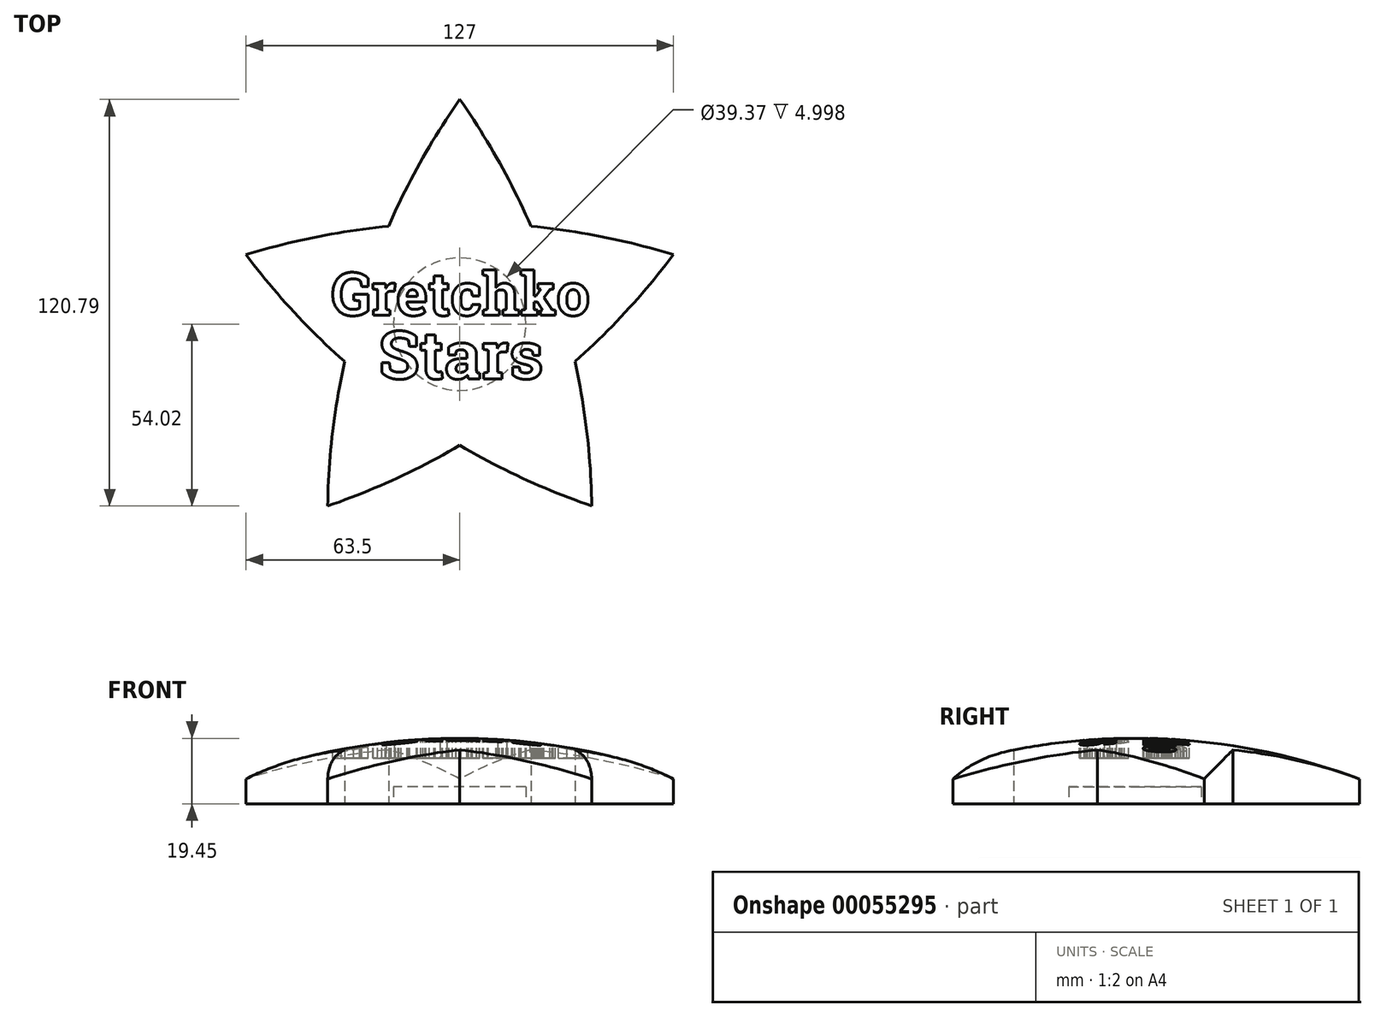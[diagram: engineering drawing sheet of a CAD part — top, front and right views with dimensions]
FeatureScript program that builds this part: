
annotation { "Feature Type Name" : "Feature", "Feature Type Description" : "" }
export const myFeature = defineFeature(function(context is Context, id is Id, definition is map)
    precondition{}
    {
        {
            var Q0;
            Q0=qCreatedBy(makeId("Top.planeOp"),FACE);
            var sketch = newSketch(context, id + "F0", { "sketchPlane" : qUnion([Q0])});
            skArc(sketch, "E0", {"start": v(39.25, -54.02) * mm, "mid": v(28.67, 9.31) * mm, "end": v(0, 66.77) * mm});
            skArc(sketch, "E1", {"start": v(0, 66.77) * mm, "mid": v(-28.67, 9.31) * mm, "end": v(-39.25, -54.02) * mm});
            skArc(sketch, "E2", {"start": v(63.5, 20.63) * mm, "mid": v(0, 30.14) * mm, "end": v(-63.5, 20.63) * mm});
            skArc(sketch, "E3", {"start": v(-63.5, 20.63) * mm, "mid": v(-17.72, -24.39) * mm, "end": v(39.25, -54.02) * mm});
            skArc(sketch, "E4", {"start": v(-39.25, -54.02) * mm, "mid": v(17.72, -24.39) * mm, "end": v(63.5, 20.63) * mm});
            skSolve(sketch);
        }
        {
            var Q0;
            Q0=qSketchRegion(id+"F0",true);
            extrude(context, id + "F1", {"entities" : qUnion([Q0]), "depth" : 67.5 * mm});
        }
        {
            var Q0;
            Q0=qCreatedBy(makeId("Top.planeOp"),FACE);
            var sketch = newSketch(context, id + "F2", { "sketchPlane" : qUnion([Q0])});
            skCircle(sketch, "E5", {"center": v(0, 0) * mm, "radius": 190.5 * mm});
            skLineSegment(sketch, "E6", {"start": v(0, 190.5) * mm, "end": v(0, -190.5) * mm});
            skSolve(sketch);
        }
        {
            var Q0;
            Q0=makeQuery(id+"F1.opExtrude","SWEPT_BODY",BODY,{"disambiguationData":[OSD([sQuery(id+"F0.wireOp",EDGE,"E0"),sQuery(id+"F0.wireOp",EDGE,"E1"),sQuery(id+"F0.wireOp",EDGE,"E2"),sQuery(id+"F0.wireOp",EDGE,"E3"),sQuery(id+"F0.wireOp",EDGE,"E4")])]});
            var Q1;
            Q1=makeQuery(id+"F1.opExtrude","SWEPT_EDGE",EDGE,{"disambiguationData":[OSD([sQuery(id+"F0.wireOp",EDGE,"E2"),sQuery(id+"F0.wireOp",EDGE,"E3")])]});
            var Q2;
            Q2=makeQuery(id+"F1.opExtrude","CAP_FACE",FACE,{"disambiguationData":[OSD([sQuery(id+"F0.wireOp",EDGE,"E0"),sQuery(id+"F0.wireOp",EDGE,"E1"),sQuery(id+"F0.wireOp",EDGE,"E2"),sQuery(id+"F0.wireOp",EDGE,"E3"),sQuery(id+"F0.wireOp",EDGE,"E4")])],"isStart":false});
            transform(context, id + "F3", {"entities" : qUnion([Q0]), "transformType" : TransformType.TRANSLATION_DISTANCE, "transformDirection" : qUnion([Q2]), "distance" : 171.05 * mm, "makeCopy" : false});
        }
        {
            var Q0;
            {var subQ0=sQuery(id+"F2.wireOp",EDGE,"E6");Q0=makeQuery(id+"F2.imprint","IMPRINT",FACE,{"disambiguationData":[TD([[makeQuery(id+"F2.imprint","IMPRINT",EDGE,{"derivedFrom":subQ0}),-1.0]])]});}
            var Q1;
            Q1=sQuery(id+"F2.wireOp",EDGE,"E6");
            revolve(context, id + "F4", {"entities" : qUnion([Q0]), "axis" : qUnion([Q1]), "revolveType" : RevolveType.FULL});
        }
        {
            var Q0;
            Q0=makeQuery(id+"F1.opExtrude","SWEPT_BODY",BODY,{"disambiguationData":[OSD([sQuery(id+"F0.wireOp",EDGE,"E0"),sQuery(id+"F0.wireOp",EDGE,"E1"),sQuery(id+"F0.wireOp",EDGE,"E2"),sQuery(id+"F0.wireOp",EDGE,"E3"),sQuery(id+"F0.wireOp",EDGE,"E4")])]});
            var Q1;
            Q1=makeQuery(id+"F4.opRevolve","SWEPT_BODY",BODY,{"disambiguationData":[OSD([sQuery(id+"F2.wireOp",EDGE,"E5"),sQuery(id+"F2.wireOp",EDGE,"E6")])]});
            booleanBodies(context, id + "F5", {"operationType" : BooleanOperationType.INTERSECTION, "tools" : qUnion([Q0, Q1])});
        }
        {
            var Q0;
            Q0=qCreatedBy(makeId("Top.planeOp"),FACE);
            var sketch = newSketch(context, id + "F6", { "sketchPlane" : qUnion([Q0])});
            skText(sketch, "E7", { "text": "Gretchko", "fontName": "RobotoSlab-Bold.ttf"});
            skLineSegment(sketch, "E8", {"start": v(0, 0) * mm, "end": v(0, 66.71) * mm});
            const initialGuessF6  = {"E7": [-0.03813, 0.00261, 1, 0, 0.0128]};
            skSetInitialGuess(sketch, initialGuessF6);
            skSolve(sketch);
        }
        {
            var Q0;
            Q0=qCreatedBy(makeId("Top.planeOp"),FACE);
            var sketch = newSketch(context, id + "F7", { "sketchPlane" : qUnion([Q0])});
            skText(sketch, "E9", { "text": "Stars", "fontName": "RobotoSlab-Bold.ttf"});
            const initialGuessF7  = {"E9": [-0.02408, -0.01622, 1, 0, 0.01428]};
            skSetInitialGuess(sketch, initialGuessF7);
            skSolve(sketch);
        }
        {
            var Q0;
            Q0=makeQuery(id+"F5.opBoolean","INTERSECT",BODY,{"derivedFrom":[makeQuery(id+"F1.opExtrude","SWEPT_BODY",BODY,{"disambiguationData":[OSD([sQuery(id+"F0.wireOp",EDGE,"E0"),sQuery(id+"F0.wireOp",EDGE,"E1"),sQuery(id+"F0.wireOp",EDGE,"E2"),sQuery(id+"F0.wireOp",EDGE,"E3"),sQuery(id+"F0.wireOp",EDGE,"E4")])]}),makeQuery(id+"F4.opRevolve","SWEPT_BODY",BODY,{"disambiguationData":[OSD([sQuery(id+"F2.wireOp",EDGE,"E5"),sQuery(id+"F2.wireOp",EDGE,"E6")])]})]});
            var Q1;
            Q1=qCreatedBy(makeId("Top.planeOp"),FACE);
            transform(context, id + "F8", {"entities" : qUnion([Q0]), "transformType" : TransformType.TRANSLATION_DISTANCE, "transformDirection" : qUnion([Q1]), "distance" : 221.94 * mm, "oppositeDirection" : true, "makeCopy" : false});
        }
        {
            var Q0;
            Q0=makeQuery(id+"F6.imprint","IMPRINT",FACE,{"disambiguationData":[TD([[makeQuery(id+"F6.imprint","IMPRINT",EDGE,{"derivedFrom":sQuery(id+"F6.wireOp",EDGE,"E7.sketch_text.stroke-0")}),-1.0]])]});
            var Q1;
            Q1=makeQuery(id+"F6.imprint","IMPRINT",FACE,{"disambiguationData":[TD([[makeQuery(id+"F6.imprint","IMPRINT",EDGE,{"derivedFrom":sQuery(id+"F6.wireOp",EDGE,"E7.sketch_text.stroke-26")}),-1.0]])]});
            var Q2;
            Q2=makeQuery(id+"F6.imprint","IMPRINT",FACE,{"disambiguationData":[TD([[makeQuery(id+"F6.imprint","IMPRINT",EDGE,{"derivedFrom":sQuery(id+"F6.wireOp",EDGE,"E7.sketch_text.stroke-69")}),-1.0]])]});
            var Q3;
            Q3=makeQuery(id+"F6.imprint","IMPRINT",FACE,{"disambiguationData":[TD([[makeQuery(id+"F6.imprint","IMPRINT",EDGE,{"derivedFrom":sQuery(id+"F6.wireOp",EDGE,"E7.sketch_text.stroke-112")}),-1.0]])]});
            var Q4;
            Q4=makeQuery(id+"F6.imprint","IMPRINT",FACE,{"disambiguationData":[TD([[makeQuery(id+"F6.imprint","IMPRINT",EDGE,{"derivedFrom":sQuery(id+"F6.wireOp",EDGE,"E7.sketch_text.stroke-138")}),-1.0]])]});
            var Q5;
            Q5=makeQuery(id+"F6.imprint","IMPRINT",FACE,{"disambiguationData":[TD([[makeQuery(id+"F6.imprint","IMPRINT",EDGE,{"derivedFrom":sQuery(id+"F6.wireOp",EDGE,"E7.sketch_text.stroke-45")}),-1.0]])]});
            var Q6;
            Q6=makeQuery(id+"F6.imprint","IMPRINT",FACE,{"disambiguationData":[TD([[makeQuery(id+"F6.imprint","IMPRINT",EDGE,{"derivedFrom":sQuery(id+"F6.wireOp",EDGE,"E7.sketch_text.stroke-89")}),-1.0]])]});
            var Q7;
            {var subQ1=sQuery(id+"F6.wireOp",EDGE,"E7.sketch_text.stroke-96");Q7=makeQuery(id+"F6.imprint","IMPRINT",FACE,{"disambiguationData":[TD([[makeQuery(id+"F6.imprint","IMPRINT",EDGE,{"derivedFrom":subQ1}),-1.0]])]});}
            var Q8;
            Q8=makeQuery(id+"F6.imprint","IMPRINT",FACE,{"disambiguationData":[TD([[makeQuery(id+"F6.imprint","IMPRINT",EDGE,{"derivedFrom":sQuery(id+"F6.wireOp",EDGE,"E7.sketch_text.stroke-165")}),-1.0]])]});
            var Q9;
            Q9=makeQuery(id+"F7.imprint","IMPRINT",FACE,{"disambiguationData":[TD([[makeQuery(id+"F7.imprint","IMPRINT",EDGE,{"derivedFrom":sQuery(id+"F7.wireOp",EDGE,"E9.sketch_text.stroke-0")}),-1.0]])]});
            var Q10;
            Q10=makeQuery(id+"F7.imprint","IMPRINT",FACE,{"disambiguationData":[TD([[makeQuery(id+"F7.imprint","IMPRINT",EDGE,{"derivedFrom":sQuery(id+"F7.wireOp",EDGE,"E9.sketch_text.stroke-30")}),-1.0]])]});
            var Q11;
            Q11=makeQuery(id+"F7.imprint","IMPRINT",FACE,{"disambiguationData":[TD([[makeQuery(id+"F7.imprint","IMPRINT",EDGE,{"derivedFrom":sQuery(id+"F7.wireOp",EDGE,"E9.sketch_text.stroke-85")}),-1.0]])]});
            var Q12;
            Q12=makeQuery(id+"F7.imprint","IMPRINT",FACE,{"disambiguationData":[TD([[makeQuery(id+"F7.imprint","IMPRINT",EDGE,{"derivedFrom":sQuery(id+"F7.wireOp",EDGE,"E9.sketch_text.stroke-104")}),-1.0]])]});
            var Q13;
            Q13=makeQuery(id+"F7.imprint","IMPRINT",FACE,{"disambiguationData":[TD([[makeQuery(id+"F7.imprint","IMPRINT",EDGE,{"derivedFrom":sQuery(id+"F7.wireOp",EDGE,"E9.sketch_text.stroke-50")}),-1.0]])]});
            var Q14;
            Q14=makeQuery(id+"FDBskpxBvZGabAj_3.imprint","IMPRINT",FACE,{"disambiguationData":[TD([[makeQuery(id+"FDBskpxBvZGabAj_3.imprint","IMPRINT",EDGE,{"derivedFrom":sQuery(id+"FDBskpxBvZGabAj_3.wireOp",EDGE,"14cc8964-4ceb-4e8c-bfe6-0e7e09cf8f31.sketch_text.stroke-0")}),-1.0]])]});
            var Q15;
            Q15=makeQuery(id+"FDBskpxBvZGabAj_3.imprint","IMPRINT",FACE,{"disambiguationData":[TD([[makeQuery(id+"FDBskpxBvZGabAj_3.imprint","IMPRINT",EDGE,{"derivedFrom":sQuery(id+"FDBskpxBvZGabAj_3.wireOp",EDGE,"14cc8964-4ceb-4e8c-bfe6-0e7e09cf8f31.sketch_text.stroke-43")}),-1.0]])]});
            var Q16;
            Q16=makeQuery(id+"FDBskpxBvZGabAj_3.imprint","IMPRINT",FACE,{"disambiguationData":[TD([[makeQuery(id+"FDBskpxBvZGabAj_3.imprint","IMPRINT",EDGE,{"derivedFrom":sQuery(id+"FDBskpxBvZGabAj_3.wireOp",EDGE,"14cc8964-4ceb-4e8c-bfe6-0e7e09cf8f31.sketch_text.stroke-53")}),-1.0]])]});
            var Q17;
            Q17=makeQuery(id+"FDBskpxBvZGabAj_3.imprint","IMPRINT",FACE,{"disambiguationData":[TD([[makeQuery(id+"FDBskpxBvZGabAj_3.imprint","IMPRINT",EDGE,{"derivedFrom":sQuery(id+"FDBskpxBvZGabAj_3.wireOp",EDGE,"14cc8964-4ceb-4e8c-bfe6-0e7e09cf8f31.sketch_text.stroke-79")}),-1.0]])]});
            var Q18;
            Q18=makeQuery(id+"FDBskpxBvZGabAj_3.imprint","IMPRINT",FACE,{"disambiguationData":[TD([[makeQuery(id+"FDBskpxBvZGabAj_3.imprint","IMPRINT",EDGE,{"derivedFrom":sQuery(id+"FDBskpxBvZGabAj_3.wireOp",EDGE,"14cc8964-4ceb-4e8c-bfe6-0e7e09cf8f31.sketch_text.stroke-83")}),-1.0]])]});
            var Q19;
            Q19=makeQuery(id+"FDBskpxBvZGabAj_3.imprint","IMPRINT",FACE,{"disambiguationData":[TD([[makeQuery(id+"FDBskpxBvZGabAj_3.imprint","IMPRINT",EDGE,{"derivedFrom":sQuery(id+"FDBskpxBvZGabAj_3.wireOp",EDGE,"14cc8964-4ceb-4e8c-bfe6-0e7e09cf8f31.sketch_text.stroke-126")}),-1.0]])]});
            var Q20;
            Q20=makeQuery(id+"FDBskpxBvZGabAj_3.imprint","IMPRINT",FACE,{"disambiguationData":[TD([[makeQuery(id+"FDBskpxBvZGabAj_3.imprint","IMPRINT",EDGE,{"derivedFrom":sQuery(id+"FDBskpxBvZGabAj_3.wireOp",EDGE,"14cc8964-4ceb-4e8c-bfe6-0e7e09cf8f31.sketch_text.stroke-23")}),-1.0]])]});
            var Q21;
            Q21=makeQuery(id+"FDBskpxBvZGabAj_3.imprint","IMPRINT",FACE,{"disambiguationData":[TD([[makeQuery(id+"FDBskpxBvZGabAj_3.imprint","IMPRINT",EDGE,{"derivedFrom":sQuery(id+"FDBskpxBvZGabAj_3.wireOp",EDGE,"14cc8964-4ceb-4e8c-bfe6-0e7e09cf8f31.sketch_text.stroke-106")}),-1.0]])]});
            var Q22;
            Q22=makeQuery(id+"FDBskpxBvZGabAj_3.imprint","IMPRINT",FACE,{"disambiguationData":[TD([[makeQuery(id+"FDBskpxBvZGabAj_3.imprint","IMPRINT",EDGE,{"derivedFrom":sQuery(id+"FDBskpxBvZGabAj_3.wireOp",EDGE,"14cc8964-4ceb-4e8c-bfe6-0e7e09cf8f31.sketch_text.stroke-136")}),-1.0]])]});
            extrude(context, id + "F9", {"entities" : qUnion([Q0, Q1, Q2, Q3, Q4, Q5, Q6, Q7, Q8, Q9, Q10, Q11, Q12, Q13, Q14, Q15, Q16, Q17, Q18, Q19, Q20, Q21, Q22]), "operationType" : NewBodyOperationType.ADD, "oppositeDirection" : true, "depth" : 15.68 * mm});
        }
        {
            var Q0;
            Q0=makeQuery(id+"F9.opExtrude","SWEPT_BODY",BODY,{"disambiguationData":[OSD([sQuery(id+"F6.wireOp",EDGE,"E7.sketch_text.stroke-0"),sQuery(id+"F6.wireOp",EDGE,"E7.sketch_text.stroke-1"),sQuery(id+"F6.wireOp",EDGE,"E7.sketch_text.stroke-2"),sQuery(id+"F6.wireOp",EDGE,"E7.sketch_text.stroke-3"),sQuery(id+"F6.wireOp",EDGE,"E7.sketch_text.stroke-4"),sQuery(id+"F6.wireOp",EDGE,"E7.sketch_text.stroke-5"),sQuery(id+"F6.wireOp",EDGE,"E7.sketch_text.stroke-6"),sQuery(id+"F6.wireOp",EDGE,"E7.sketch_text.stroke-7"),sQuery(id+"F6.wireOp",EDGE,"E7.sketch_text.stroke-8"),sQuery(id+"F6.wireOp",EDGE,"E7.sketch_text.stroke-9"),sQuery(id+"F6.wireOp",EDGE,"E7.sketch_text.stroke-10"),sQuery(id+"F6.wireOp",EDGE,"E7.sketch_text.stroke-11"),sQuery(id+"F6.wireOp",EDGE,"E7.sketch_text.stroke-12"),sQuery(id+"F6.wireOp",EDGE,"E7.sketch_text.stroke-13"),sQuery(id+"F6.wireOp",EDGE,"E7.sketch_text.stroke-14"),sQuery(id+"F6.wireOp",EDGE,"E7.sketch_text.stroke-15"),sQuery(id+"F6.wireOp",EDGE,"E7.sketch_text.stroke-16"),sQuery(id+"F6.wireOp",EDGE,"E7.sketch_text.stroke-17"),sQuery(id+"F6.wireOp",EDGE,"E7.sketch_text.stroke-18"),sQuery(id+"F6.wireOp",EDGE,"E7.sketch_text.stroke-19"),sQuery(id+"F6.wireOp",EDGE,"E7.sketch_text.stroke-20"),sQuery(id+"F6.wireOp",EDGE,"E7.sketch_text.stroke-21"),sQuery(id+"F6.wireOp",EDGE,"E7.sketch_text.stroke-22"),sQuery(id+"F6.wireOp",EDGE,"E7.sketch_text.stroke-23"),sQuery(id+"F6.wireOp",EDGE,"E7.sketch_text.stroke-24"),sQuery(id+"F6.wireOp",EDGE,"E7.sketch_text.stroke-25")])]});
            var Q1;
            Q1=makeQuery(id+"F9.opExtrude","SWEPT_BODY",BODY,{"disambiguationData":[OSD([sQuery(id+"F6.wireOp",EDGE,"E7.sketch_text.stroke-26"),sQuery(id+"F6.wireOp",EDGE,"E7.sketch_text.stroke-27"),sQuery(id+"F6.wireOp",EDGE,"E7.sketch_text.stroke-28"),sQuery(id+"F6.wireOp",EDGE,"E7.sketch_text.stroke-29"),sQuery(id+"F6.wireOp",EDGE,"E7.sketch_text.stroke-30"),sQuery(id+"F6.wireOp",EDGE,"E7.sketch_text.stroke-31"),sQuery(id+"F6.wireOp",EDGE,"E7.sketch_text.stroke-32"),sQuery(id+"F6.wireOp",EDGE,"E7.sketch_text.stroke-33"),sQuery(id+"F6.wireOp",EDGE,"E7.sketch_text.stroke-34"),sQuery(id+"F6.wireOp",EDGE,"E7.sketch_text.stroke-35"),sQuery(id+"F6.wireOp",EDGE,"E7.sketch_text.stroke-36"),sQuery(id+"F6.wireOp",EDGE,"E7.sketch_text.stroke-37"),sQuery(id+"F6.wireOp",EDGE,"E7.sketch_text.stroke-38"),sQuery(id+"F6.wireOp",EDGE,"E7.sketch_text.stroke-39"),sQuery(id+"F6.wireOp",EDGE,"E7.sketch_text.stroke-40"),sQuery(id+"F6.wireOp",EDGE,"E7.sketch_text.stroke-41"),sQuery(id+"F6.wireOp",EDGE,"E7.sketch_text.stroke-42"),sQuery(id+"F6.wireOp",EDGE,"E7.sketch_text.stroke-43"),sQuery(id+"F6.wireOp",EDGE,"E7.sketch_text.stroke-44")])]});
            var Q2;
            Q2=makeQuery(id+"F9.opExtrude","SWEPT_BODY",BODY,{"disambiguationData":[OSD([sQuery(id+"F6.wireOp",EDGE,"E7.sketch_text.stroke-45"),sQuery(id+"F6.wireOp",EDGE,"E7.sketch_text.stroke-46"),sQuery(id+"F6.wireOp",EDGE,"E7.sketch_text.stroke-47"),sQuery(id+"F6.wireOp",EDGE,"E7.sketch_text.stroke-48"),sQuery(id+"F6.wireOp",EDGE,"E7.sketch_text.stroke-49"),sQuery(id+"F6.wireOp",EDGE,"E7.sketch_text.stroke-50"),sQuery(id+"F6.wireOp",EDGE,"E7.sketch_text.stroke-51"),sQuery(id+"F6.wireOp",EDGE,"E7.sketch_text.stroke-52"),sQuery(id+"F6.wireOp",EDGE,"E7.sketch_text.stroke-53"),sQuery(id+"F6.wireOp",EDGE,"E7.sketch_text.stroke-54"),sQuery(id+"F6.wireOp",EDGE,"E7.sketch_text.stroke-55"),sQuery(id+"F6.wireOp",EDGE,"E7.sketch_text.stroke-56"),sQuery(id+"F6.wireOp",EDGE,"E7.sketch_text.stroke-57"),sQuery(id+"F6.wireOp",EDGE,"E7.sketch_text.stroke-58"),sQuery(id+"F6.wireOp",EDGE,"E7.sketch_text.stroke-59"),sQuery(id+"F6.wireOp",EDGE,"E7.sketch_text.stroke-60"),sQuery(id+"F6.wireOp",EDGE,"E7.sketch_text.stroke-61"),sQuery(id+"F6.wireOp",EDGE,"E7.sketch_text.stroke-62"),sQuery(id+"F6.wireOp",EDGE,"E7.sketch_text.stroke-63"),sQuery(id+"F6.wireOp",EDGE,"E7.sketch_text.stroke-64"),sQuery(id+"F6.wireOp",EDGE,"E7.sketch_text.stroke-65"),sQuery(id+"F6.wireOp",EDGE,"E7.sketch_text.stroke-66"),sQuery(id+"F6.wireOp",EDGE,"E7.sketch_text.stroke-67"),sQuery(id+"F6.wireOp",EDGE,"E7.sketch_text.stroke-68")])]});
            var Q3;
            Q3=makeQuery(id+"F9.opExtrude","SWEPT_BODY",BODY,{"disambiguationData":[OSD([sQuery(id+"F6.wireOp",EDGE,"E7.sketch_text.stroke-69"),sQuery(id+"F6.wireOp",EDGE,"E7.sketch_text.stroke-70"),sQuery(id+"F6.wireOp",EDGE,"E7.sketch_text.stroke-71"),sQuery(id+"F6.wireOp",EDGE,"E7.sketch_text.stroke-72"),sQuery(id+"F6.wireOp",EDGE,"E7.sketch_text.stroke-73"),sQuery(id+"F6.wireOp",EDGE,"E7.sketch_text.stroke-74"),sQuery(id+"F6.wireOp",EDGE,"E7.sketch_text.stroke-75"),sQuery(id+"F6.wireOp",EDGE,"E7.sketch_text.stroke-76"),sQuery(id+"F6.wireOp",EDGE,"E7.sketch_text.stroke-77"),sQuery(id+"F6.wireOp",EDGE,"E7.sketch_text.stroke-78"),sQuery(id+"F6.wireOp",EDGE,"E7.sketch_text.stroke-79"),sQuery(id+"F6.wireOp",EDGE,"E7.sketch_text.stroke-80"),sQuery(id+"F6.wireOp",EDGE,"E7.sketch_text.stroke-81"),sQuery(id+"F6.wireOp",EDGE,"E7.sketch_text.stroke-82"),sQuery(id+"F6.wireOp",EDGE,"E7.sketch_text.stroke-83"),sQuery(id+"F6.wireOp",EDGE,"E7.sketch_text.stroke-84"),sQuery(id+"F6.wireOp",EDGE,"E7.sketch_text.stroke-85"),sQuery(id+"F6.wireOp",EDGE,"E7.sketch_text.stroke-86"),sQuery(id+"F6.wireOp",EDGE,"E7.sketch_text.stroke-87"),sQuery(id+"F6.wireOp",EDGE,"E7.sketch_text.stroke-88")])]});
            var Q4;
            Q4=makeQuery(id+"F9.opExtrude","SWEPT_BODY",BODY,{"disambiguationData":[OSD([sQuery(id+"F6.wireOp",EDGE,"E7.sketch_text.stroke-89"),sQuery(id+"F6.wireOp",EDGE,"E7.sketch_text.stroke-90"),sQuery(id+"F6.wireOp",EDGE,"E7.sketch_text.stroke-91"),sQuery(id+"F6.wireOp",EDGE,"E7.sketch_text.stroke-92"),sQuery(id+"F6.wireOp",EDGE,"E7.sketch_text.stroke-93"),sQuery(id+"F6.wireOp",EDGE,"E7.sketch_text.stroke-94"),sQuery(id+"F6.wireOp",EDGE,"E7.sketch_text.stroke-95"),sQuery(id+"F6.wireOp",EDGE,"E7.sketch_text.stroke-96"),sQuery(id+"F6.wireOp",EDGE,"E7.sketch_text.stroke-97"),sQuery(id+"F6.wireOp",EDGE,"E7.sketch_text.stroke-98"),sQuery(id+"F6.wireOp",EDGE,"E7.sketch_text.stroke-99"),sQuery(id+"F6.wireOp",EDGE,"E7.sketch_text.stroke-100"),sQuery(id+"F6.wireOp",EDGE,"E7.sketch_text.stroke-101"),sQuery(id+"F6.wireOp",EDGE,"E7.sketch_text.stroke-102"),sQuery(id+"F6.wireOp",EDGE,"E7.sketch_text.stroke-103"),sQuery(id+"F6.wireOp",EDGE,"E7.sketch_text.stroke-104"),sQuery(id+"F6.wireOp",EDGE,"E7.sketch_text.stroke-105"),sQuery(id+"F6.wireOp",EDGE,"E7.sketch_text.stroke-106"),sQuery(id+"F6.wireOp",EDGE,"E7.sketch_text.stroke-107"),sQuery(id+"F6.wireOp",EDGE,"E7.sketch_text.stroke-108"),sQuery(id+"F6.wireOp",EDGE,"E7.sketch_text.stroke-109"),sQuery(id+"F6.wireOp",EDGE,"E7.sketch_text.stroke-110"),sQuery(id+"F6.wireOp",EDGE,"E7.sketch_text.stroke-111")])]});
            var Q5;
            Q5=makeQuery(id+"F9.opExtrude","SWEPT_BODY",BODY,{"disambiguationData":[OSD([sQuery(id+"F6.wireOp",EDGE,"E7.sketch_text.stroke-112"),sQuery(id+"F6.wireOp",EDGE,"E7.sketch_text.stroke-113"),sQuery(id+"F6.wireOp",EDGE,"E7.sketch_text.stroke-114"),sQuery(id+"F6.wireOp",EDGE,"E7.sketch_text.stroke-115"),sQuery(id+"F6.wireOp",EDGE,"E7.sketch_text.stroke-116"),sQuery(id+"F6.wireOp",EDGE,"E7.sketch_text.stroke-117"),sQuery(id+"F6.wireOp",EDGE,"E7.sketch_text.stroke-118"),sQuery(id+"F6.wireOp",EDGE,"E7.sketch_text.stroke-119"),sQuery(id+"F6.wireOp",EDGE,"E7.sketch_text.stroke-120"),sQuery(id+"F6.wireOp",EDGE,"E7.sketch_text.stroke-121"),sQuery(id+"F6.wireOp",EDGE,"E7.sketch_text.stroke-122"),sQuery(id+"F6.wireOp",EDGE,"E7.sketch_text.stroke-123"),sQuery(id+"F6.wireOp",EDGE,"E7.sketch_text.stroke-124"),sQuery(id+"F6.wireOp",EDGE,"E7.sketch_text.stroke-125"),sQuery(id+"F6.wireOp",EDGE,"E7.sketch_text.stroke-126"),sQuery(id+"F6.wireOp",EDGE,"E7.sketch_text.stroke-127"),sQuery(id+"F6.wireOp",EDGE,"E7.sketch_text.stroke-128"),sQuery(id+"F6.wireOp",EDGE,"E7.sketch_text.stroke-129"),sQuery(id+"F6.wireOp",EDGE,"E7.sketch_text.stroke-130"),sQuery(id+"F6.wireOp",EDGE,"E7.sketch_text.stroke-131"),sQuery(id+"F6.wireOp",EDGE,"E7.sketch_text.stroke-132"),sQuery(id+"F6.wireOp",EDGE,"E7.sketch_text.stroke-133"),sQuery(id+"F6.wireOp",EDGE,"E7.sketch_text.stroke-134"),sQuery(id+"F6.wireOp",EDGE,"E7.sketch_text.stroke-135"),sQuery(id+"F6.wireOp",EDGE,"E7.sketch_text.stroke-136"),sQuery(id+"F6.wireOp",EDGE,"E7.sketch_text.stroke-137")])]});
            var Q6;
            Q6=makeQuery(id+"F9.opExtrude","SWEPT_BODY",BODY,{"disambiguationData":[OSD([sQuery(id+"F6.wireOp",EDGE,"E7.sketch_text.stroke-138"),sQuery(id+"F6.wireOp",EDGE,"E7.sketch_text.stroke-139"),sQuery(id+"F6.wireOp",EDGE,"E7.sketch_text.stroke-140"),sQuery(id+"F6.wireOp",EDGE,"E7.sketch_text.stroke-141"),sQuery(id+"F6.wireOp",EDGE,"E7.sketch_text.stroke-142"),sQuery(id+"F6.wireOp",EDGE,"E7.sketch_text.stroke-143"),sQuery(id+"F6.wireOp",EDGE,"E7.sketch_text.stroke-144"),sQuery(id+"F6.wireOp",EDGE,"E7.sketch_text.stroke-145"),sQuery(id+"F6.wireOp",EDGE,"E7.sketch_text.stroke-146"),sQuery(id+"F6.wireOp",EDGE,"E7.sketch_text.stroke-147"),sQuery(id+"F6.wireOp",EDGE,"E7.sketch_text.stroke-148"),sQuery(id+"F6.wireOp",EDGE,"E7.sketch_text.stroke-149"),sQuery(id+"F6.wireOp",EDGE,"E7.sketch_text.stroke-150"),sQuery(id+"F6.wireOp",EDGE,"E7.sketch_text.stroke-151"),sQuery(id+"F6.wireOp",EDGE,"E7.sketch_text.stroke-152"),sQuery(id+"F6.wireOp",EDGE,"E7.sketch_text.stroke-153"),sQuery(id+"F6.wireOp",EDGE,"E7.sketch_text.stroke-154"),sQuery(id+"F6.wireOp",EDGE,"E7.sketch_text.stroke-155"),sQuery(id+"F6.wireOp",EDGE,"E7.sketch_text.stroke-156"),sQuery(id+"F6.wireOp",EDGE,"E7.sketch_text.stroke-157"),sQuery(id+"F6.wireOp",EDGE,"E7.sketch_text.stroke-158"),sQuery(id+"F6.wireOp",EDGE,"E7.sketch_text.stroke-159"),sQuery(id+"F6.wireOp",EDGE,"E7.sketch_text.stroke-160"),sQuery(id+"F6.wireOp",EDGE,"E7.sketch_text.stroke-161"),sQuery(id+"F6.wireOp",EDGE,"E7.sketch_text.stroke-162"),sQuery(id+"F6.wireOp",EDGE,"E7.sketch_text.stroke-163"),sQuery(id+"F6.wireOp",EDGE,"E7.sketch_text.stroke-164")])]});
            var Q7;
            Q7=makeQuery(id+"F9.opExtrude","SWEPT_BODY",BODY,{"disambiguationData":[OSD([sQuery(id+"F6.wireOp",EDGE,"E7.sketch_text.stroke-165"),sQuery(id+"F6.wireOp",EDGE,"E7.sketch_text.stroke-166"),sQuery(id+"F6.wireOp",EDGE,"E7.sketch_text.stroke-167"),sQuery(id+"F6.wireOp",EDGE,"E7.sketch_text.stroke-168"),sQuery(id+"F6.wireOp",EDGE,"E7.sketch_text.stroke-169"),sQuery(id+"F6.wireOp",EDGE,"E7.sketch_text.stroke-170"),sQuery(id+"F6.wireOp",EDGE,"E7.sketch_text.stroke-171"),sQuery(id+"F6.wireOp",EDGE,"E7.sketch_text.stroke-172"),sQuery(id+"F6.wireOp",EDGE,"E7.sketch_text.stroke-173"),sQuery(id+"F6.wireOp",EDGE,"E7.sketch_text.stroke-174"),sQuery(id+"F6.wireOp",EDGE,"E7.sketch_text.stroke-175"),sQuery(id+"F6.wireOp",EDGE,"E7.sketch_text.stroke-176"),sQuery(id+"F6.wireOp",EDGE,"E7.sketch_text.stroke-177"),sQuery(id+"F6.wireOp",EDGE,"E7.sketch_text.stroke-178"),sQuery(id+"F6.wireOp",EDGE,"E7.sketch_text.stroke-179"),sQuery(id+"F6.wireOp",EDGE,"E7.sketch_text.stroke-180"),sQuery(id+"F6.wireOp",EDGE,"E7.sketch_text.stroke-181"),sQuery(id+"F6.wireOp",EDGE,"E7.sketch_text.stroke-182"),sQuery(id+"F6.wireOp",EDGE,"E7.sketch_text.stroke-183"),sQuery(id+"F6.wireOp",EDGE,"E7.sketch_text.stroke-184")])]});
            var Q8;
            Q8=makeQuery(id+"F9.opExtrude","SWEPT_BODY",BODY,{"disambiguationData":[OSD([sQuery(id+"F7.wireOp",EDGE,"E9.sketch_text.stroke-0"),sQuery(id+"F7.wireOp",EDGE,"E9.sketch_text.stroke-1"),sQuery(id+"F7.wireOp",EDGE,"E9.sketch_text.stroke-2"),sQuery(id+"F7.wireOp",EDGE,"E9.sketch_text.stroke-3"),sQuery(id+"F7.wireOp",EDGE,"E9.sketch_text.stroke-4"),sQuery(id+"F7.wireOp",EDGE,"E9.sketch_text.stroke-5"),sQuery(id+"F7.wireOp",EDGE,"E9.sketch_text.stroke-6"),sQuery(id+"F7.wireOp",EDGE,"E9.sketch_text.stroke-7"),sQuery(id+"F7.wireOp",EDGE,"E9.sketch_text.stroke-8"),sQuery(id+"F7.wireOp",EDGE,"E9.sketch_text.stroke-9"),sQuery(id+"F7.wireOp",EDGE,"E9.sketch_text.stroke-10"),sQuery(id+"F7.wireOp",EDGE,"E9.sketch_text.stroke-11"),sQuery(id+"F7.wireOp",EDGE,"E9.sketch_text.stroke-12"),sQuery(id+"F7.wireOp",EDGE,"E9.sketch_text.stroke-13"),sQuery(id+"F7.wireOp",EDGE,"E9.sketch_text.stroke-14"),sQuery(id+"F7.wireOp",EDGE,"E9.sketch_text.stroke-15"),sQuery(id+"F7.wireOp",EDGE,"E9.sketch_text.stroke-16"),sQuery(id+"F7.wireOp",EDGE,"E9.sketch_text.stroke-17"),sQuery(id+"F7.wireOp",EDGE,"E9.sketch_text.stroke-18"),sQuery(id+"F7.wireOp",EDGE,"E9.sketch_text.stroke-19"),sQuery(id+"F7.wireOp",EDGE,"E9.sketch_text.stroke-20"),sQuery(id+"F7.wireOp",EDGE,"E9.sketch_text.stroke-21"),sQuery(id+"F7.wireOp",EDGE,"E9.sketch_text.stroke-22"),sQuery(id+"F7.wireOp",EDGE,"E9.sketch_text.stroke-23"),sQuery(id+"F7.wireOp",EDGE,"E9.sketch_text.stroke-24"),sQuery(id+"F7.wireOp",EDGE,"E9.sketch_text.stroke-25"),sQuery(id+"F7.wireOp",EDGE,"E9.sketch_text.stroke-26"),sQuery(id+"F7.wireOp",EDGE,"E9.sketch_text.stroke-27"),sQuery(id+"F7.wireOp",EDGE,"E9.sketch_text.stroke-28"),sQuery(id+"F7.wireOp",EDGE,"E9.sketch_text.stroke-29")])]});
            var Q9;
            Q9=makeQuery(id+"F9.opExtrude","SWEPT_BODY",BODY,{"disambiguationData":[OSD([sQuery(id+"F7.wireOp",EDGE,"E9.sketch_text.stroke-30"),sQuery(id+"F7.wireOp",EDGE,"E9.sketch_text.stroke-31"),sQuery(id+"F7.wireOp",EDGE,"E9.sketch_text.stroke-32"),sQuery(id+"F7.wireOp",EDGE,"E9.sketch_text.stroke-33"),sQuery(id+"F7.wireOp",EDGE,"E9.sketch_text.stroke-34"),sQuery(id+"F7.wireOp",EDGE,"E9.sketch_text.stroke-35"),sQuery(id+"F7.wireOp",EDGE,"E9.sketch_text.stroke-36"),sQuery(id+"F7.wireOp",EDGE,"E9.sketch_text.stroke-37"),sQuery(id+"F7.wireOp",EDGE,"E9.sketch_text.stroke-38"),sQuery(id+"F7.wireOp",EDGE,"E9.sketch_text.stroke-39"),sQuery(id+"F7.wireOp",EDGE,"E9.sketch_text.stroke-40"),sQuery(id+"F7.wireOp",EDGE,"E9.sketch_text.stroke-41"),sQuery(id+"F7.wireOp",EDGE,"E9.sketch_text.stroke-42"),sQuery(id+"F7.wireOp",EDGE,"E9.sketch_text.stroke-43"),sQuery(id+"F7.wireOp",EDGE,"E9.sketch_text.stroke-44"),sQuery(id+"F7.wireOp",EDGE,"E9.sketch_text.stroke-45"),sQuery(id+"F7.wireOp",EDGE,"E9.sketch_text.stroke-46"),sQuery(id+"F7.wireOp",EDGE,"E9.sketch_text.stroke-47"),sQuery(id+"F7.wireOp",EDGE,"E9.sketch_text.stroke-48"),sQuery(id+"F7.wireOp",EDGE,"E9.sketch_text.stroke-49")])]});
            var Q10;
            Q10=makeQuery(id+"F9.opExtrude","SWEPT_BODY",BODY,{"disambiguationData":[OSD([sQuery(id+"F7.wireOp",EDGE,"E9.sketch_text.stroke-50"),sQuery(id+"F7.wireOp",EDGE,"E9.sketch_text.stroke-51"),sQuery(id+"F7.wireOp",EDGE,"E9.sketch_text.stroke-52"),sQuery(id+"F7.wireOp",EDGE,"E9.sketch_text.stroke-53"),sQuery(id+"F7.wireOp",EDGE,"E9.sketch_text.stroke-54"),sQuery(id+"F7.wireOp",EDGE,"E9.sketch_text.stroke-55"),sQuery(id+"F7.wireOp",EDGE,"E9.sketch_text.stroke-56"),sQuery(id+"F7.wireOp",EDGE,"E9.sketch_text.stroke-57"),sQuery(id+"F7.wireOp",EDGE,"E9.sketch_text.stroke-58"),sQuery(id+"F7.wireOp",EDGE,"E9.sketch_text.stroke-59"),sQuery(id+"F7.wireOp",EDGE,"E9.sketch_text.stroke-60"),sQuery(id+"F7.wireOp",EDGE,"E9.sketch_text.stroke-61"),sQuery(id+"F7.wireOp",EDGE,"E9.sketch_text.stroke-62"),sQuery(id+"F7.wireOp",EDGE,"E9.sketch_text.stroke-63"),sQuery(id+"F7.wireOp",EDGE,"E9.sketch_text.stroke-64"),sQuery(id+"F7.wireOp",EDGE,"E9.sketch_text.stroke-65"),sQuery(id+"F7.wireOp",EDGE,"E9.sketch_text.stroke-66"),sQuery(id+"F7.wireOp",EDGE,"E9.sketch_text.stroke-67"),sQuery(id+"F7.wireOp",EDGE,"E9.sketch_text.stroke-68"),sQuery(id+"F7.wireOp",EDGE,"E9.sketch_text.stroke-69"),sQuery(id+"F7.wireOp",EDGE,"E9.sketch_text.stroke-70"),sQuery(id+"F7.wireOp",EDGE,"E9.sketch_text.stroke-71"),sQuery(id+"F7.wireOp",EDGE,"E9.sketch_text.stroke-72"),sQuery(id+"F7.wireOp",EDGE,"E9.sketch_text.stroke-73"),sQuery(id+"F7.wireOp",EDGE,"E9.sketch_text.stroke-74"),sQuery(id+"F7.wireOp",EDGE,"E9.sketch_text.stroke-75"),sQuery(id+"F7.wireOp",EDGE,"E9.sketch_text.stroke-76"),sQuery(id+"F7.wireOp",EDGE,"E9.sketch_text.stroke-77"),sQuery(id+"F7.wireOp",EDGE,"E9.sketch_text.stroke-78"),sQuery(id+"F7.wireOp",EDGE,"E9.sketch_text.stroke-79"),sQuery(id+"F7.wireOp",EDGE,"E9.sketch_text.stroke-80"),sQuery(id+"F7.wireOp",EDGE,"E9.sketch_text.stroke-81"),sQuery(id+"F7.wireOp",EDGE,"E9.sketch_text.stroke-82"),sQuery(id+"F7.wireOp",EDGE,"E9.sketch_text.stroke-83"),sQuery(id+"F7.wireOp",EDGE,"E9.sketch_text.stroke-84")])]});
            var Q11;
            Q11=makeQuery(id+"F9.opExtrude","SWEPT_BODY",BODY,{"disambiguationData":[OSD([sQuery(id+"F7.wireOp",EDGE,"E9.sketch_text.stroke-85"),sQuery(id+"F7.wireOp",EDGE,"E9.sketch_text.stroke-86"),sQuery(id+"F7.wireOp",EDGE,"E9.sketch_text.stroke-87"),sQuery(id+"F7.wireOp",EDGE,"E9.sketch_text.stroke-88"),sQuery(id+"F7.wireOp",EDGE,"E9.sketch_text.stroke-89"),sQuery(id+"F7.wireOp",EDGE,"E9.sketch_text.stroke-90"),sQuery(id+"F7.wireOp",EDGE,"E9.sketch_text.stroke-91"),sQuery(id+"F7.wireOp",EDGE,"E9.sketch_text.stroke-92"),sQuery(id+"F7.wireOp",EDGE,"E9.sketch_text.stroke-93"),sQuery(id+"F7.wireOp",EDGE,"E9.sketch_text.stroke-94"),sQuery(id+"F7.wireOp",EDGE,"E9.sketch_text.stroke-95"),sQuery(id+"F7.wireOp",EDGE,"E9.sketch_text.stroke-96"),sQuery(id+"F7.wireOp",EDGE,"E9.sketch_text.stroke-97"),sQuery(id+"F7.wireOp",EDGE,"E9.sketch_text.stroke-98"),sQuery(id+"F7.wireOp",EDGE,"E9.sketch_text.stroke-99"),sQuery(id+"F7.wireOp",EDGE,"E9.sketch_text.stroke-100"),sQuery(id+"F7.wireOp",EDGE,"E9.sketch_text.stroke-101"),sQuery(id+"F7.wireOp",EDGE,"E9.sketch_text.stroke-102"),sQuery(id+"F7.wireOp",EDGE,"E9.sketch_text.stroke-103")])]});
            var Q12;
            Q12=makeQuery(id+"F9.opExtrude","SWEPT_BODY",BODY,{"disambiguationData":[OSD([sQuery(id+"F7.wireOp",EDGE,"E9.sketch_text.stroke-104"),sQuery(id+"F7.wireOp",EDGE,"E9.sketch_text.stroke-105"),sQuery(id+"F7.wireOp",EDGE,"E9.sketch_text.stroke-106"),sQuery(id+"F7.wireOp",EDGE,"E9.sketch_text.stroke-107"),sQuery(id+"F7.wireOp",EDGE,"E9.sketch_text.stroke-108"),sQuery(id+"F7.wireOp",EDGE,"E9.sketch_text.stroke-109"),sQuery(id+"F7.wireOp",EDGE,"E9.sketch_text.stroke-110"),sQuery(id+"F7.wireOp",EDGE,"E9.sketch_text.stroke-111"),sQuery(id+"F7.wireOp",EDGE,"E9.sketch_text.stroke-112"),sQuery(id+"F7.wireOp",EDGE,"E9.sketch_text.stroke-113"),sQuery(id+"F7.wireOp",EDGE,"E9.sketch_text.stroke-114"),sQuery(id+"F7.wireOp",EDGE,"E9.sketch_text.stroke-115"),sQuery(id+"F7.wireOp",EDGE,"E9.sketch_text.stroke-116"),sQuery(id+"F7.wireOp",EDGE,"E9.sketch_text.stroke-117"),sQuery(id+"F7.wireOp",EDGE,"E9.sketch_text.stroke-118"),sQuery(id+"F7.wireOp",EDGE,"E9.sketch_text.stroke-119"),sQuery(id+"F7.wireOp",EDGE,"E9.sketch_text.stroke-120"),sQuery(id+"F7.wireOp",EDGE,"E9.sketch_text.stroke-121"),sQuery(id+"F7.wireOp",EDGE,"E9.sketch_text.stroke-122"),sQuery(id+"F7.wireOp",EDGE,"E9.sketch_text.stroke-123"),sQuery(id+"F7.wireOp",EDGE,"E9.sketch_text.stroke-124"),sQuery(id+"F7.wireOp",EDGE,"E9.sketch_text.stroke-125"),sQuery(id+"F7.wireOp",EDGE,"E9.sketch_text.stroke-126"),sQuery(id+"F7.wireOp",EDGE,"E9.sketch_text.stroke-127"),sQuery(id+"F7.wireOp",EDGE,"E9.sketch_text.stroke-128"),sQuery(id+"F7.wireOp",EDGE,"E9.sketch_text.stroke-129"),sQuery(id+"F7.wireOp",EDGE,"E9.sketch_text.stroke-130"),sQuery(id+"F7.wireOp",EDGE,"E9.sketch_text.stroke-131"),sQuery(id+"F7.wireOp",EDGE,"E9.sketch_text.stroke-132"),sQuery(id+"F7.wireOp",EDGE,"E9.sketch_text.stroke-133")])]});
            var Q13;
            Q13=makeQuery(id+"F9.opExtrude","SWEPT_BODY",BODY,{"disambiguationData":[OSD([sQuery(id+"FDBskpxBvZGabAj_3.wireOp",EDGE,"14cc8964-4ceb-4e8c-bfe6-0e7e09cf8f31.sketch_text.stroke-0"),sQuery(id+"FDBskpxBvZGabAj_3.wireOp",EDGE,"14cc8964-4ceb-4e8c-bfe6-0e7e09cf8f31.sketch_text.stroke-1"),sQuery(id+"FDBskpxBvZGabAj_3.wireOp",EDGE,"14cc8964-4ceb-4e8c-bfe6-0e7e09cf8f31.sketch_text.stroke-2"),sQuery(id+"FDBskpxBvZGabAj_3.wireOp",EDGE,"14cc8964-4ceb-4e8c-bfe6-0e7e09cf8f31.sketch_text.stroke-3"),sQuery(id+"FDBskpxBvZGabAj_3.wireOp",EDGE,"14cc8964-4ceb-4e8c-bfe6-0e7e09cf8f31.sketch_text.stroke-4"),sQuery(id+"FDBskpxBvZGabAj_3.wireOp",EDGE,"14cc8964-4ceb-4e8c-bfe6-0e7e09cf8f31.sketch_text.stroke-5"),sQuery(id+"FDBskpxBvZGabAj_3.wireOp",EDGE,"14cc8964-4ceb-4e8c-bfe6-0e7e09cf8f31.sketch_text.stroke-6"),sQuery(id+"FDBskpxBvZGabAj_3.wireOp",EDGE,"14cc8964-4ceb-4e8c-bfe6-0e7e09cf8f31.sketch_text.stroke-7"),sQuery(id+"FDBskpxBvZGabAj_3.wireOp",EDGE,"14cc8964-4ceb-4e8c-bfe6-0e7e09cf8f31.sketch_text.stroke-8"),sQuery(id+"FDBskpxBvZGabAj_3.wireOp",EDGE,"14cc8964-4ceb-4e8c-bfe6-0e7e09cf8f31.sketch_text.stroke-9"),sQuery(id+"FDBskpxBvZGabAj_3.wireOp",EDGE,"14cc8964-4ceb-4e8c-bfe6-0e7e09cf8f31.sketch_text.stroke-10"),sQuery(id+"FDBskpxBvZGabAj_3.wireOp",EDGE,"14cc8964-4ceb-4e8c-bfe6-0e7e09cf8f31.sketch_text.stroke-11"),sQuery(id+"FDBskpxBvZGabAj_3.wireOp",EDGE,"14cc8964-4ceb-4e8c-bfe6-0e7e09cf8f31.sketch_text.stroke-12"),sQuery(id+"FDBskpxBvZGabAj_3.wireOp",EDGE,"14cc8964-4ceb-4e8c-bfe6-0e7e09cf8f31.sketch_text.stroke-13"),sQuery(id+"FDBskpxBvZGabAj_3.wireOp",EDGE,"14cc8964-4ceb-4e8c-bfe6-0e7e09cf8f31.sketch_text.stroke-14"),sQuery(id+"FDBskpxBvZGabAj_3.wireOp",EDGE,"14cc8964-4ceb-4e8c-bfe6-0e7e09cf8f31.sketch_text.stroke-15"),sQuery(id+"FDBskpxBvZGabAj_3.wireOp",EDGE,"14cc8964-4ceb-4e8c-bfe6-0e7e09cf8f31.sketch_text.stroke-16"),sQuery(id+"FDBskpxBvZGabAj_3.wireOp",EDGE,"14cc8964-4ceb-4e8c-bfe6-0e7e09cf8f31.sketch_text.stroke-17"),sQuery(id+"FDBskpxBvZGabAj_3.wireOp",EDGE,"14cc8964-4ceb-4e8c-bfe6-0e7e09cf8f31.sketch_text.stroke-18"),sQuery(id+"FDBskpxBvZGabAj_3.wireOp",EDGE,"14cc8964-4ceb-4e8c-bfe6-0e7e09cf8f31.sketch_text.stroke-19"),sQuery(id+"FDBskpxBvZGabAj_3.wireOp",EDGE,"14cc8964-4ceb-4e8c-bfe6-0e7e09cf8f31.sketch_text.stroke-20"),sQuery(id+"FDBskpxBvZGabAj_3.wireOp",EDGE,"14cc8964-4ceb-4e8c-bfe6-0e7e09cf8f31.sketch_text.stroke-21"),sQuery(id+"FDBskpxBvZGabAj_3.wireOp",EDGE,"14cc8964-4ceb-4e8c-bfe6-0e7e09cf8f31.sketch_text.stroke-22")])]});
            var Q14;
            Q14=makeQuery(id+"F9.opExtrude","SWEPT_BODY",BODY,{"disambiguationData":[OSD([sQuery(id+"FDBskpxBvZGabAj_3.wireOp",EDGE,"14cc8964-4ceb-4e8c-bfe6-0e7e09cf8f31.sketch_text.stroke-23"),sQuery(id+"FDBskpxBvZGabAj_3.wireOp",EDGE,"14cc8964-4ceb-4e8c-bfe6-0e7e09cf8f31.sketch_text.stroke-24"),sQuery(id+"FDBskpxBvZGabAj_3.wireOp",EDGE,"14cc8964-4ceb-4e8c-bfe6-0e7e09cf8f31.sketch_text.stroke-25"),sQuery(id+"FDBskpxBvZGabAj_3.wireOp",EDGE,"14cc8964-4ceb-4e8c-bfe6-0e7e09cf8f31.sketch_text.stroke-26"),sQuery(id+"FDBskpxBvZGabAj_3.wireOp",EDGE,"14cc8964-4ceb-4e8c-bfe6-0e7e09cf8f31.sketch_text.stroke-27"),sQuery(id+"FDBskpxBvZGabAj_3.wireOp",EDGE,"14cc8964-4ceb-4e8c-bfe6-0e7e09cf8f31.sketch_text.stroke-28"),sQuery(id+"FDBskpxBvZGabAj_3.wireOp",EDGE,"14cc8964-4ceb-4e8c-bfe6-0e7e09cf8f31.sketch_text.stroke-29"),sQuery(id+"FDBskpxBvZGabAj_3.wireOp",EDGE,"14cc8964-4ceb-4e8c-bfe6-0e7e09cf8f31.sketch_text.stroke-30"),sQuery(id+"FDBskpxBvZGabAj_3.wireOp",EDGE,"14cc8964-4ceb-4e8c-bfe6-0e7e09cf8f31.sketch_text.stroke-31"),sQuery(id+"FDBskpxBvZGabAj_3.wireOp",EDGE,"14cc8964-4ceb-4e8c-bfe6-0e7e09cf8f31.sketch_text.stroke-32"),sQuery(id+"FDBskpxBvZGabAj_3.wireOp",EDGE,"14cc8964-4ceb-4e8c-bfe6-0e7e09cf8f31.sketch_text.stroke-33"),sQuery(id+"FDBskpxBvZGabAj_3.wireOp",EDGE,"14cc8964-4ceb-4e8c-bfe6-0e7e09cf8f31.sketch_text.stroke-34"),sQuery(id+"FDBskpxBvZGabAj_3.wireOp",EDGE,"14cc8964-4ceb-4e8c-bfe6-0e7e09cf8f31.sketch_text.stroke-35"),sQuery(id+"FDBskpxBvZGabAj_3.wireOp",EDGE,"14cc8964-4ceb-4e8c-bfe6-0e7e09cf8f31.sketch_text.stroke-36"),sQuery(id+"FDBskpxBvZGabAj_3.wireOp",EDGE,"14cc8964-4ceb-4e8c-bfe6-0e7e09cf8f31.sketch_text.stroke-37"),sQuery(id+"FDBskpxBvZGabAj_3.wireOp",EDGE,"14cc8964-4ceb-4e8c-bfe6-0e7e09cf8f31.sketch_text.stroke-38"),sQuery(id+"FDBskpxBvZGabAj_3.wireOp",EDGE,"14cc8964-4ceb-4e8c-bfe6-0e7e09cf8f31.sketch_text.stroke-39"),sQuery(id+"FDBskpxBvZGabAj_3.wireOp",EDGE,"14cc8964-4ceb-4e8c-bfe6-0e7e09cf8f31.sketch_text.stroke-40"),sQuery(id+"FDBskpxBvZGabAj_3.wireOp",EDGE,"14cc8964-4ceb-4e8c-bfe6-0e7e09cf8f31.sketch_text.stroke-41"),sQuery(id+"FDBskpxBvZGabAj_3.wireOp",EDGE,"14cc8964-4ceb-4e8c-bfe6-0e7e09cf8f31.sketch_text.stroke-42")])]});
            var Q15;
            Q15=makeQuery(id+"F9.opExtrude","SWEPT_BODY",BODY,{"disambiguationData":[OSD([sQuery(id+"FDBskpxBvZGabAj_3.wireOp",EDGE,"14cc8964-4ceb-4e8c-bfe6-0e7e09cf8f31.sketch_text.stroke-43"),sQuery(id+"FDBskpxBvZGabAj_3.wireOp",EDGE,"14cc8964-4ceb-4e8c-bfe6-0e7e09cf8f31.sketch_text.stroke-44"),sQuery(id+"FDBskpxBvZGabAj_3.wireOp",EDGE,"14cc8964-4ceb-4e8c-bfe6-0e7e09cf8f31.sketch_text.stroke-45"),sQuery(id+"FDBskpxBvZGabAj_3.wireOp",EDGE,"14cc8964-4ceb-4e8c-bfe6-0e7e09cf8f31.sketch_text.stroke-46"),sQuery(id+"FDBskpxBvZGabAj_3.wireOp",EDGE,"14cc8964-4ceb-4e8c-bfe6-0e7e09cf8f31.sketch_text.stroke-47"),sQuery(id+"FDBskpxBvZGabAj_3.wireOp",EDGE,"14cc8964-4ceb-4e8c-bfe6-0e7e09cf8f31.sketch_text.stroke-48"),sQuery(id+"FDBskpxBvZGabAj_3.wireOp",EDGE,"14cc8964-4ceb-4e8c-bfe6-0e7e09cf8f31.sketch_text.stroke-49"),sQuery(id+"FDBskpxBvZGabAj_3.wireOp",EDGE,"14cc8964-4ceb-4e8c-bfe6-0e7e09cf8f31.sketch_text.stroke-50"),sQuery(id+"FDBskpxBvZGabAj_3.wireOp",EDGE,"14cc8964-4ceb-4e8c-bfe6-0e7e09cf8f31.sketch_text.stroke-51"),sQuery(id+"FDBskpxBvZGabAj_3.wireOp",EDGE,"14cc8964-4ceb-4e8c-bfe6-0e7e09cf8f31.sketch_text.stroke-52")])]});
            var Q16;
            Q16=makeQuery(id+"F9.opExtrude","SWEPT_BODY",BODY,{"disambiguationData":[OSD([sQuery(id+"FDBskpxBvZGabAj_3.wireOp",EDGE,"14cc8964-4ceb-4e8c-bfe6-0e7e09cf8f31.sketch_text.stroke-53"),sQuery(id+"FDBskpxBvZGabAj_3.wireOp",EDGE,"14cc8964-4ceb-4e8c-bfe6-0e7e09cf8f31.sketch_text.stroke-54"),sQuery(id+"FDBskpxBvZGabAj_3.wireOp",EDGE,"14cc8964-4ceb-4e8c-bfe6-0e7e09cf8f31.sketch_text.stroke-55"),sQuery(id+"FDBskpxBvZGabAj_3.wireOp",EDGE,"14cc8964-4ceb-4e8c-bfe6-0e7e09cf8f31.sketch_text.stroke-56"),sQuery(id+"FDBskpxBvZGabAj_3.wireOp",EDGE,"14cc8964-4ceb-4e8c-bfe6-0e7e09cf8f31.sketch_text.stroke-57"),sQuery(id+"FDBskpxBvZGabAj_3.wireOp",EDGE,"14cc8964-4ceb-4e8c-bfe6-0e7e09cf8f31.sketch_text.stroke-58"),sQuery(id+"FDBskpxBvZGabAj_3.wireOp",EDGE,"14cc8964-4ceb-4e8c-bfe6-0e7e09cf8f31.sketch_text.stroke-59"),sQuery(id+"FDBskpxBvZGabAj_3.wireOp",EDGE,"14cc8964-4ceb-4e8c-bfe6-0e7e09cf8f31.sketch_text.stroke-60"),sQuery(id+"FDBskpxBvZGabAj_3.wireOp",EDGE,"14cc8964-4ceb-4e8c-bfe6-0e7e09cf8f31.sketch_text.stroke-61"),sQuery(id+"FDBskpxBvZGabAj_3.wireOp",EDGE,"14cc8964-4ceb-4e8c-bfe6-0e7e09cf8f31.sketch_text.stroke-62"),sQuery(id+"FDBskpxBvZGabAj_3.wireOp",EDGE,"14cc8964-4ceb-4e8c-bfe6-0e7e09cf8f31.sketch_text.stroke-63"),sQuery(id+"FDBskpxBvZGabAj_3.wireOp",EDGE,"14cc8964-4ceb-4e8c-bfe6-0e7e09cf8f31.sketch_text.stroke-64"),sQuery(id+"FDBskpxBvZGabAj_3.wireOp",EDGE,"14cc8964-4ceb-4e8c-bfe6-0e7e09cf8f31.sketch_text.stroke-65"),sQuery(id+"FDBskpxBvZGabAj_3.wireOp",EDGE,"14cc8964-4ceb-4e8c-bfe6-0e7e09cf8f31.sketch_text.stroke-66"),sQuery(id+"FDBskpxBvZGabAj_3.wireOp",EDGE,"14cc8964-4ceb-4e8c-bfe6-0e7e09cf8f31.sketch_text.stroke-67"),sQuery(id+"FDBskpxBvZGabAj_3.wireOp",EDGE,"14cc8964-4ceb-4e8c-bfe6-0e7e09cf8f31.sketch_text.stroke-68"),sQuery(id+"FDBskpxBvZGabAj_3.wireOp",EDGE,"14cc8964-4ceb-4e8c-bfe6-0e7e09cf8f31.sketch_text.stroke-69"),sQuery(id+"FDBskpxBvZGabAj_3.wireOp",EDGE,"14cc8964-4ceb-4e8c-bfe6-0e7e09cf8f31.sketch_text.stroke-70"),sQuery(id+"FDBskpxBvZGabAj_3.wireOp",EDGE,"14cc8964-4ceb-4e8c-bfe6-0e7e09cf8f31.sketch_text.stroke-71"),sQuery(id+"FDBskpxBvZGabAj_3.wireOp",EDGE,"14cc8964-4ceb-4e8c-bfe6-0e7e09cf8f31.sketch_text.stroke-72"),sQuery(id+"FDBskpxBvZGabAj_3.wireOp",EDGE,"14cc8964-4ceb-4e8c-bfe6-0e7e09cf8f31.sketch_text.stroke-73"),sQuery(id+"FDBskpxBvZGabAj_3.wireOp",EDGE,"14cc8964-4ceb-4e8c-bfe6-0e7e09cf8f31.sketch_text.stroke-74"),sQuery(id+"FDBskpxBvZGabAj_3.wireOp",EDGE,"14cc8964-4ceb-4e8c-bfe6-0e7e09cf8f31.sketch_text.stroke-75"),sQuery(id+"FDBskpxBvZGabAj_3.wireOp",EDGE,"14cc8964-4ceb-4e8c-bfe6-0e7e09cf8f31.sketch_text.stroke-76"),sQuery(id+"FDBskpxBvZGabAj_3.wireOp",EDGE,"14cc8964-4ceb-4e8c-bfe6-0e7e09cf8f31.sketch_text.stroke-77"),sQuery(id+"FDBskpxBvZGabAj_3.wireOp",EDGE,"14cc8964-4ceb-4e8c-bfe6-0e7e09cf8f31.sketch_text.stroke-78")])]});
            var Q17;
            Q17=makeQuery(id+"F9.opExtrude","SWEPT_BODY",BODY,{"disambiguationData":[OSD([sQuery(id+"FDBskpxBvZGabAj_3.wireOp",EDGE,"14cc8964-4ceb-4e8c-bfe6-0e7e09cf8f31.sketch_text.stroke-79"),sQuery(id+"FDBskpxBvZGabAj_3.wireOp",EDGE,"14cc8964-4ceb-4e8c-bfe6-0e7e09cf8f31.sketch_text.stroke-80"),sQuery(id+"FDBskpxBvZGabAj_3.wireOp",EDGE,"14cc8964-4ceb-4e8c-bfe6-0e7e09cf8f31.sketch_text.stroke-81"),sQuery(id+"FDBskpxBvZGabAj_3.wireOp",EDGE,"14cc8964-4ceb-4e8c-bfe6-0e7e09cf8f31.sketch_text.stroke-82")])]});
            var Q18;
            Q18=makeQuery(id+"F9.opExtrude","SWEPT_BODY",BODY,{"disambiguationData":[OSD([sQuery(id+"FDBskpxBvZGabAj_3.wireOp",EDGE,"14cc8964-4ceb-4e8c-bfe6-0e7e09cf8f31.sketch_text.stroke-83"),sQuery(id+"FDBskpxBvZGabAj_3.wireOp",EDGE,"14cc8964-4ceb-4e8c-bfe6-0e7e09cf8f31.sketch_text.stroke-84"),sQuery(id+"FDBskpxBvZGabAj_3.wireOp",EDGE,"14cc8964-4ceb-4e8c-bfe6-0e7e09cf8f31.sketch_text.stroke-85"),sQuery(id+"FDBskpxBvZGabAj_3.wireOp",EDGE,"14cc8964-4ceb-4e8c-bfe6-0e7e09cf8f31.sketch_text.stroke-86"),sQuery(id+"FDBskpxBvZGabAj_3.wireOp",EDGE,"14cc8964-4ceb-4e8c-bfe6-0e7e09cf8f31.sketch_text.stroke-87"),sQuery(id+"FDBskpxBvZGabAj_3.wireOp",EDGE,"14cc8964-4ceb-4e8c-bfe6-0e7e09cf8f31.sketch_text.stroke-88"),sQuery(id+"FDBskpxBvZGabAj_3.wireOp",EDGE,"14cc8964-4ceb-4e8c-bfe6-0e7e09cf8f31.sketch_text.stroke-89"),sQuery(id+"FDBskpxBvZGabAj_3.wireOp",EDGE,"14cc8964-4ceb-4e8c-bfe6-0e7e09cf8f31.sketch_text.stroke-90"),sQuery(id+"FDBskpxBvZGabAj_3.wireOp",EDGE,"14cc8964-4ceb-4e8c-bfe6-0e7e09cf8f31.sketch_text.stroke-91"),sQuery(id+"FDBskpxBvZGabAj_3.wireOp",EDGE,"14cc8964-4ceb-4e8c-bfe6-0e7e09cf8f31.sketch_text.stroke-92"),sQuery(id+"FDBskpxBvZGabAj_3.wireOp",EDGE,"14cc8964-4ceb-4e8c-bfe6-0e7e09cf8f31.sketch_text.stroke-93"),sQuery(id+"FDBskpxBvZGabAj_3.wireOp",EDGE,"14cc8964-4ceb-4e8c-bfe6-0e7e09cf8f31.sketch_text.stroke-94"),sQuery(id+"FDBskpxBvZGabAj_3.wireOp",EDGE,"14cc8964-4ceb-4e8c-bfe6-0e7e09cf8f31.sketch_text.stroke-95"),sQuery(id+"FDBskpxBvZGabAj_3.wireOp",EDGE,"14cc8964-4ceb-4e8c-bfe6-0e7e09cf8f31.sketch_text.stroke-96"),sQuery(id+"FDBskpxBvZGabAj_3.wireOp",EDGE,"14cc8964-4ceb-4e8c-bfe6-0e7e09cf8f31.sketch_text.stroke-97"),sQuery(id+"FDBskpxBvZGabAj_3.wireOp",EDGE,"14cc8964-4ceb-4e8c-bfe6-0e7e09cf8f31.sketch_text.stroke-98"),sQuery(id+"FDBskpxBvZGabAj_3.wireOp",EDGE,"14cc8964-4ceb-4e8c-bfe6-0e7e09cf8f31.sketch_text.stroke-99"),sQuery(id+"FDBskpxBvZGabAj_3.wireOp",EDGE,"14cc8964-4ceb-4e8c-bfe6-0e7e09cf8f31.sketch_text.stroke-100"),sQuery(id+"FDBskpxBvZGabAj_3.wireOp",EDGE,"14cc8964-4ceb-4e8c-bfe6-0e7e09cf8f31.sketch_text.stroke-101"),sQuery(id+"FDBskpxBvZGabAj_3.wireOp",EDGE,"14cc8964-4ceb-4e8c-bfe6-0e7e09cf8f31.sketch_text.stroke-102"),sQuery(id+"FDBskpxBvZGabAj_3.wireOp",EDGE,"14cc8964-4ceb-4e8c-bfe6-0e7e09cf8f31.sketch_text.stroke-103"),sQuery(id+"FDBskpxBvZGabAj_3.wireOp",EDGE,"14cc8964-4ceb-4e8c-bfe6-0e7e09cf8f31.sketch_text.stroke-104"),sQuery(id+"FDBskpxBvZGabAj_3.wireOp",EDGE,"14cc8964-4ceb-4e8c-bfe6-0e7e09cf8f31.sketch_text.stroke-105")])]});
            var Q19;
            Q19=makeQuery(id+"F9.opExtrude","SWEPT_BODY",BODY,{"disambiguationData":[OSD([sQuery(id+"FDBskpxBvZGabAj_3.wireOp",EDGE,"14cc8964-4ceb-4e8c-bfe6-0e7e09cf8f31.sketch_text.stroke-106"),sQuery(id+"FDBskpxBvZGabAj_3.wireOp",EDGE,"14cc8964-4ceb-4e8c-bfe6-0e7e09cf8f31.sketch_text.stroke-107"),sQuery(id+"FDBskpxBvZGabAj_3.wireOp",EDGE,"14cc8964-4ceb-4e8c-bfe6-0e7e09cf8f31.sketch_text.stroke-108"),sQuery(id+"FDBskpxBvZGabAj_3.wireOp",EDGE,"14cc8964-4ceb-4e8c-bfe6-0e7e09cf8f31.sketch_text.stroke-109"),sQuery(id+"FDBskpxBvZGabAj_3.wireOp",EDGE,"14cc8964-4ceb-4e8c-bfe6-0e7e09cf8f31.sketch_text.stroke-110"),sQuery(id+"FDBskpxBvZGabAj_3.wireOp",EDGE,"14cc8964-4ceb-4e8c-bfe6-0e7e09cf8f31.sketch_text.stroke-111"),sQuery(id+"FDBskpxBvZGabAj_3.wireOp",EDGE,"14cc8964-4ceb-4e8c-bfe6-0e7e09cf8f31.sketch_text.stroke-112"),sQuery(id+"FDBskpxBvZGabAj_3.wireOp",EDGE,"14cc8964-4ceb-4e8c-bfe6-0e7e09cf8f31.sketch_text.stroke-113"),sQuery(id+"FDBskpxBvZGabAj_3.wireOp",EDGE,"14cc8964-4ceb-4e8c-bfe6-0e7e09cf8f31.sketch_text.stroke-114"),sQuery(id+"FDBskpxBvZGabAj_3.wireOp",EDGE,"14cc8964-4ceb-4e8c-bfe6-0e7e09cf8f31.sketch_text.stroke-115"),sQuery(id+"FDBskpxBvZGabAj_3.wireOp",EDGE,"14cc8964-4ceb-4e8c-bfe6-0e7e09cf8f31.sketch_text.stroke-116"),sQuery(id+"FDBskpxBvZGabAj_3.wireOp",EDGE,"14cc8964-4ceb-4e8c-bfe6-0e7e09cf8f31.sketch_text.stroke-117"),sQuery(id+"FDBskpxBvZGabAj_3.wireOp",EDGE,"14cc8964-4ceb-4e8c-bfe6-0e7e09cf8f31.sketch_text.stroke-118"),sQuery(id+"FDBskpxBvZGabAj_3.wireOp",EDGE,"14cc8964-4ceb-4e8c-bfe6-0e7e09cf8f31.sketch_text.stroke-119"),sQuery(id+"FDBskpxBvZGabAj_3.wireOp",EDGE,"14cc8964-4ceb-4e8c-bfe6-0e7e09cf8f31.sketch_text.stroke-120"),sQuery(id+"FDBskpxBvZGabAj_3.wireOp",EDGE,"14cc8964-4ceb-4e8c-bfe6-0e7e09cf8f31.sketch_text.stroke-121"),sQuery(id+"FDBskpxBvZGabAj_3.wireOp",EDGE,"14cc8964-4ceb-4e8c-bfe6-0e7e09cf8f31.sketch_text.stroke-122"),sQuery(id+"FDBskpxBvZGabAj_3.wireOp",EDGE,"14cc8964-4ceb-4e8c-bfe6-0e7e09cf8f31.sketch_text.stroke-123"),sQuery(id+"FDBskpxBvZGabAj_3.wireOp",EDGE,"14cc8964-4ceb-4e8c-bfe6-0e7e09cf8f31.sketch_text.stroke-124"),sQuery(id+"FDBskpxBvZGabAj_3.wireOp",EDGE,"14cc8964-4ceb-4e8c-bfe6-0e7e09cf8f31.sketch_text.stroke-125")])]});
            var Q20;
            Q20=makeQuery(id+"F9.opExtrude","SWEPT_BODY",BODY,{"disambiguationData":[OSD([sQuery(id+"FDBskpxBvZGabAj_3.wireOp",EDGE,"14cc8964-4ceb-4e8c-bfe6-0e7e09cf8f31.sketch_text.stroke-126"),sQuery(id+"FDBskpxBvZGabAj_3.wireOp",EDGE,"14cc8964-4ceb-4e8c-bfe6-0e7e09cf8f31.sketch_text.stroke-127"),sQuery(id+"FDBskpxBvZGabAj_3.wireOp",EDGE,"14cc8964-4ceb-4e8c-bfe6-0e7e09cf8f31.sketch_text.stroke-128"),sQuery(id+"FDBskpxBvZGabAj_3.wireOp",EDGE,"14cc8964-4ceb-4e8c-bfe6-0e7e09cf8f31.sketch_text.stroke-129"),sQuery(id+"FDBskpxBvZGabAj_3.wireOp",EDGE,"14cc8964-4ceb-4e8c-bfe6-0e7e09cf8f31.sketch_text.stroke-130"),sQuery(id+"FDBskpxBvZGabAj_3.wireOp",EDGE,"14cc8964-4ceb-4e8c-bfe6-0e7e09cf8f31.sketch_text.stroke-131"),sQuery(id+"FDBskpxBvZGabAj_3.wireOp",EDGE,"14cc8964-4ceb-4e8c-bfe6-0e7e09cf8f31.sketch_text.stroke-132"),sQuery(id+"FDBskpxBvZGabAj_3.wireOp",EDGE,"14cc8964-4ceb-4e8c-bfe6-0e7e09cf8f31.sketch_text.stroke-133"),sQuery(id+"FDBskpxBvZGabAj_3.wireOp",EDGE,"14cc8964-4ceb-4e8c-bfe6-0e7e09cf8f31.sketch_text.stroke-134"),sQuery(id+"FDBskpxBvZGabAj_3.wireOp",EDGE,"14cc8964-4ceb-4e8c-bfe6-0e7e09cf8f31.sketch_text.stroke-135")])]});
            var Q21;
            Q21=makeQuery(id+"F9.opExtrude","SWEPT_BODY",BODY,{"disambiguationData":[OSD([sQuery(id+"FDBskpxBvZGabAj_3.wireOp",EDGE,"14cc8964-4ceb-4e8c-bfe6-0e7e09cf8f31.sketch_text.stroke-136"),sQuery(id+"FDBskpxBvZGabAj_3.wireOp",EDGE,"14cc8964-4ceb-4e8c-bfe6-0e7e09cf8f31.sketch_text.stroke-137"),sQuery(id+"FDBskpxBvZGabAj_3.wireOp",EDGE,"14cc8964-4ceb-4e8c-bfe6-0e7e09cf8f31.sketch_text.stroke-138"),sQuery(id+"FDBskpxBvZGabAj_3.wireOp",EDGE,"14cc8964-4ceb-4e8c-bfe6-0e7e09cf8f31.sketch_text.stroke-139"),sQuery(id+"FDBskpxBvZGabAj_3.wireOp",EDGE,"14cc8964-4ceb-4e8c-bfe6-0e7e09cf8f31.sketch_text.stroke-140"),sQuery(id+"FDBskpxBvZGabAj_3.wireOp",EDGE,"14cc8964-4ceb-4e8c-bfe6-0e7e09cf8f31.sketch_text.stroke-141"),sQuery(id+"FDBskpxBvZGabAj_3.wireOp",EDGE,"14cc8964-4ceb-4e8c-bfe6-0e7e09cf8f31.sketch_text.stroke-142"),sQuery(id+"FDBskpxBvZGabAj_3.wireOp",EDGE,"14cc8964-4ceb-4e8c-bfe6-0e7e09cf8f31.sketch_text.stroke-143"),sQuery(id+"FDBskpxBvZGabAj_3.wireOp",EDGE,"14cc8964-4ceb-4e8c-bfe6-0e7e09cf8f31.sketch_text.stroke-144"),sQuery(id+"FDBskpxBvZGabAj_3.wireOp",EDGE,"14cc8964-4ceb-4e8c-bfe6-0e7e09cf8f31.sketch_text.stroke-145"),sQuery(id+"FDBskpxBvZGabAj_3.wireOp",EDGE,"14cc8964-4ceb-4e8c-bfe6-0e7e09cf8f31.sketch_text.stroke-146"),sQuery(id+"FDBskpxBvZGabAj_3.wireOp",EDGE,"14cc8964-4ceb-4e8c-bfe6-0e7e09cf8f31.sketch_text.stroke-147"),sQuery(id+"FDBskpxBvZGabAj_3.wireOp",EDGE,"14cc8964-4ceb-4e8c-bfe6-0e7e09cf8f31.sketch_text.stroke-148"),sQuery(id+"FDBskpxBvZGabAj_3.wireOp",EDGE,"14cc8964-4ceb-4e8c-bfe6-0e7e09cf8f31.sketch_text.stroke-149"),sQuery(id+"FDBskpxBvZGabAj_3.wireOp",EDGE,"14cc8964-4ceb-4e8c-bfe6-0e7e09cf8f31.sketch_text.stroke-150"),sQuery(id+"FDBskpxBvZGabAj_3.wireOp",EDGE,"14cc8964-4ceb-4e8c-bfe6-0e7e09cf8f31.sketch_text.stroke-151"),sQuery(id+"FDBskpxBvZGabAj_3.wireOp",EDGE,"14cc8964-4ceb-4e8c-bfe6-0e7e09cf8f31.sketch_text.stroke-152"),sQuery(id+"FDBskpxBvZGabAj_3.wireOp",EDGE,"14cc8964-4ceb-4e8c-bfe6-0e7e09cf8f31.sketch_text.stroke-153"),sQuery(id+"FDBskpxBvZGabAj_3.wireOp",EDGE,"14cc8964-4ceb-4e8c-bfe6-0e7e09cf8f31.sketch_text.stroke-154"),sQuery(id+"FDBskpxBvZGabAj_3.wireOp",EDGE,"14cc8964-4ceb-4e8c-bfe6-0e7e09cf8f31.sketch_text.stroke-155"),sQuery(id+"FDBskpxBvZGabAj_3.wireOp",EDGE,"14cc8964-4ceb-4e8c-bfe6-0e7e09cf8f31.sketch_text.stroke-156"),sQuery(id+"FDBskpxBvZGabAj_3.wireOp",EDGE,"14cc8964-4ceb-4e8c-bfe6-0e7e09cf8f31.sketch_text.stroke-157"),sQuery(id+"FDBskpxBvZGabAj_3.wireOp",EDGE,"14cc8964-4ceb-4e8c-bfe6-0e7e09cf8f31.sketch_text.stroke-158"),sQuery(id+"FDBskpxBvZGabAj_3.wireOp",EDGE,"14cc8964-4ceb-4e8c-bfe6-0e7e09cf8f31.sketch_text.stroke-159"),sQuery(id+"FDBskpxBvZGabAj_3.wireOp",EDGE,"14cc8964-4ceb-4e8c-bfe6-0e7e09cf8f31.sketch_text.stroke-160"),sQuery(id+"FDBskpxBvZGabAj_3.wireOp",EDGE,"14cc8964-4ceb-4e8c-bfe6-0e7e09cf8f31.sketch_text.stroke-161"),sQuery(id+"FDBskpxBvZGabAj_3.wireOp",EDGE,"14cc8964-4ceb-4e8c-bfe6-0e7e09cf8f31.sketch_text.stroke-162"),sQuery(id+"FDBskpxBvZGabAj_3.wireOp",EDGE,"14cc8964-4ceb-4e8c-bfe6-0e7e09cf8f31.sketch_text.stroke-163")])]});
            var Q22;
            Q22=qCreatedBy(makeId("Top.planeOp"),FACE);
            transform(context, id + "F10", {"entities" : qUnion([Q0, Q1, Q2, Q3, Q4, Q5, Q6, Q7, Q8, Q9, Q10, Q11, Q12, Q13, Q14, Q15, Q16, Q17, Q18, Q19, Q20, Q21]), "transformType" : TransformType.TRANSLATION_DISTANCE, "transformDirection" : qUnion([Q22]), "distance" : 21.66 * mm, "oppositeDirection" : true, "makeCopy" : false});
        }
        {
            var Q0;
            Q0=makeQuery(id+"F9.opExtrude","SWEPT_BODY",BODY,{"disambiguationData":[OSD([sQuery(id+"F6.wireOp",EDGE,"E7.sketch_text.stroke-0"),sQuery(id+"F6.wireOp",EDGE,"E7.sketch_text.stroke-1"),sQuery(id+"F6.wireOp",EDGE,"E7.sketch_text.stroke-2"),sQuery(id+"F6.wireOp",EDGE,"E7.sketch_text.stroke-3"),sQuery(id+"F6.wireOp",EDGE,"E7.sketch_text.stroke-4"),sQuery(id+"F6.wireOp",EDGE,"E7.sketch_text.stroke-5"),sQuery(id+"F6.wireOp",EDGE,"E7.sketch_text.stroke-6"),sQuery(id+"F6.wireOp",EDGE,"E7.sketch_text.stroke-7"),sQuery(id+"F6.wireOp",EDGE,"E7.sketch_text.stroke-8"),sQuery(id+"F6.wireOp",EDGE,"E7.sketch_text.stroke-9"),sQuery(id+"F6.wireOp",EDGE,"E7.sketch_text.stroke-10"),sQuery(id+"F6.wireOp",EDGE,"E7.sketch_text.stroke-11"),sQuery(id+"F6.wireOp",EDGE,"E7.sketch_text.stroke-12"),sQuery(id+"F6.wireOp",EDGE,"E7.sketch_text.stroke-13"),sQuery(id+"F6.wireOp",EDGE,"E7.sketch_text.stroke-14"),sQuery(id+"F6.wireOp",EDGE,"E7.sketch_text.stroke-15"),sQuery(id+"F6.wireOp",EDGE,"E7.sketch_text.stroke-16"),sQuery(id+"F6.wireOp",EDGE,"E7.sketch_text.stroke-17"),sQuery(id+"F6.wireOp",EDGE,"E7.sketch_text.stroke-18"),sQuery(id+"F6.wireOp",EDGE,"E7.sketch_text.stroke-19"),sQuery(id+"F6.wireOp",EDGE,"E7.sketch_text.stroke-20"),sQuery(id+"F6.wireOp",EDGE,"E7.sketch_text.stroke-21"),sQuery(id+"F6.wireOp",EDGE,"E7.sketch_text.stroke-22"),sQuery(id+"F6.wireOp",EDGE,"E7.sketch_text.stroke-23"),sQuery(id+"F6.wireOp",EDGE,"E7.sketch_text.stroke-24"),sQuery(id+"F6.wireOp",EDGE,"E7.sketch_text.stroke-25")])]});
            var Q1;
            Q1=makeQuery(id+"F9.opExtrude","SWEPT_BODY",BODY,{"disambiguationData":[OSD([sQuery(id+"F6.wireOp",EDGE,"E7.sketch_text.stroke-26"),sQuery(id+"F6.wireOp",EDGE,"E7.sketch_text.stroke-27"),sQuery(id+"F6.wireOp",EDGE,"E7.sketch_text.stroke-28"),sQuery(id+"F6.wireOp",EDGE,"E7.sketch_text.stroke-29"),sQuery(id+"F6.wireOp",EDGE,"E7.sketch_text.stroke-30"),sQuery(id+"F6.wireOp",EDGE,"E7.sketch_text.stroke-31"),sQuery(id+"F6.wireOp",EDGE,"E7.sketch_text.stroke-32"),sQuery(id+"F6.wireOp",EDGE,"E7.sketch_text.stroke-33"),sQuery(id+"F6.wireOp",EDGE,"E7.sketch_text.stroke-34"),sQuery(id+"F6.wireOp",EDGE,"E7.sketch_text.stroke-35"),sQuery(id+"F6.wireOp",EDGE,"E7.sketch_text.stroke-36"),sQuery(id+"F6.wireOp",EDGE,"E7.sketch_text.stroke-37"),sQuery(id+"F6.wireOp",EDGE,"E7.sketch_text.stroke-38"),sQuery(id+"F6.wireOp",EDGE,"E7.sketch_text.stroke-39"),sQuery(id+"F6.wireOp",EDGE,"E7.sketch_text.stroke-40"),sQuery(id+"F6.wireOp",EDGE,"E7.sketch_text.stroke-41"),sQuery(id+"F6.wireOp",EDGE,"E7.sketch_text.stroke-42"),sQuery(id+"F6.wireOp",EDGE,"E7.sketch_text.stroke-43"),sQuery(id+"F6.wireOp",EDGE,"E7.sketch_text.stroke-44")])]});
            var Q2;
            Q2=makeQuery(id+"F9.opExtrude","SWEPT_BODY",BODY,{"disambiguationData":[OSD([sQuery(id+"F6.wireOp",EDGE,"E7.sketch_text.stroke-45"),sQuery(id+"F6.wireOp",EDGE,"E7.sketch_text.stroke-46"),sQuery(id+"F6.wireOp",EDGE,"E7.sketch_text.stroke-47"),sQuery(id+"F6.wireOp",EDGE,"E7.sketch_text.stroke-48"),sQuery(id+"F6.wireOp",EDGE,"E7.sketch_text.stroke-49"),sQuery(id+"F6.wireOp",EDGE,"E7.sketch_text.stroke-50"),sQuery(id+"F6.wireOp",EDGE,"E7.sketch_text.stroke-51"),sQuery(id+"F6.wireOp",EDGE,"E7.sketch_text.stroke-52"),sQuery(id+"F6.wireOp",EDGE,"E7.sketch_text.stroke-53"),sQuery(id+"F6.wireOp",EDGE,"E7.sketch_text.stroke-54"),sQuery(id+"F6.wireOp",EDGE,"E7.sketch_text.stroke-55"),sQuery(id+"F6.wireOp",EDGE,"E7.sketch_text.stroke-56"),sQuery(id+"F6.wireOp",EDGE,"E7.sketch_text.stroke-57"),sQuery(id+"F6.wireOp",EDGE,"E7.sketch_text.stroke-58"),sQuery(id+"F6.wireOp",EDGE,"E7.sketch_text.stroke-59"),sQuery(id+"F6.wireOp",EDGE,"E7.sketch_text.stroke-60"),sQuery(id+"F6.wireOp",EDGE,"E7.sketch_text.stroke-61"),sQuery(id+"F6.wireOp",EDGE,"E7.sketch_text.stroke-62"),sQuery(id+"F6.wireOp",EDGE,"E7.sketch_text.stroke-63"),sQuery(id+"F6.wireOp",EDGE,"E7.sketch_text.stroke-64"),sQuery(id+"F6.wireOp",EDGE,"E7.sketch_text.stroke-65"),sQuery(id+"F6.wireOp",EDGE,"E7.sketch_text.stroke-66"),sQuery(id+"F6.wireOp",EDGE,"E7.sketch_text.stroke-67"),sQuery(id+"F6.wireOp",EDGE,"E7.sketch_text.stroke-68")])]});
            var Q3;
            Q3=makeQuery(id+"F9.opExtrude","SWEPT_BODY",BODY,{"disambiguationData":[OSD([sQuery(id+"F6.wireOp",EDGE,"E7.sketch_text.stroke-69"),sQuery(id+"F6.wireOp",EDGE,"E7.sketch_text.stroke-70"),sQuery(id+"F6.wireOp",EDGE,"E7.sketch_text.stroke-71"),sQuery(id+"F6.wireOp",EDGE,"E7.sketch_text.stroke-72"),sQuery(id+"F6.wireOp",EDGE,"E7.sketch_text.stroke-73"),sQuery(id+"F6.wireOp",EDGE,"E7.sketch_text.stroke-74"),sQuery(id+"F6.wireOp",EDGE,"E7.sketch_text.stroke-75"),sQuery(id+"F6.wireOp",EDGE,"E7.sketch_text.stroke-76"),sQuery(id+"F6.wireOp",EDGE,"E7.sketch_text.stroke-77"),sQuery(id+"F6.wireOp",EDGE,"E7.sketch_text.stroke-78"),sQuery(id+"F6.wireOp",EDGE,"E7.sketch_text.stroke-79"),sQuery(id+"F6.wireOp",EDGE,"E7.sketch_text.stroke-80"),sQuery(id+"F6.wireOp",EDGE,"E7.sketch_text.stroke-81"),sQuery(id+"F6.wireOp",EDGE,"E7.sketch_text.stroke-82"),sQuery(id+"F6.wireOp",EDGE,"E7.sketch_text.stroke-83"),sQuery(id+"F6.wireOp",EDGE,"E7.sketch_text.stroke-84"),sQuery(id+"F6.wireOp",EDGE,"E7.sketch_text.stroke-85"),sQuery(id+"F6.wireOp",EDGE,"E7.sketch_text.stroke-86"),sQuery(id+"F6.wireOp",EDGE,"E7.sketch_text.stroke-87"),sQuery(id+"F6.wireOp",EDGE,"E7.sketch_text.stroke-88")])]});
            var Q4;
            Q4=makeQuery(id+"F9.opExtrude","SWEPT_BODY",BODY,{"disambiguationData":[OSD([sQuery(id+"F6.wireOp",EDGE,"E7.sketch_text.stroke-89"),sQuery(id+"F6.wireOp",EDGE,"E7.sketch_text.stroke-90"),sQuery(id+"F6.wireOp",EDGE,"E7.sketch_text.stroke-91"),sQuery(id+"F6.wireOp",EDGE,"E7.sketch_text.stroke-92"),sQuery(id+"F6.wireOp",EDGE,"E7.sketch_text.stroke-93"),sQuery(id+"F6.wireOp",EDGE,"E7.sketch_text.stroke-94"),sQuery(id+"F6.wireOp",EDGE,"E7.sketch_text.stroke-95"),sQuery(id+"F6.wireOp",EDGE,"E7.sketch_text.stroke-96"),sQuery(id+"F6.wireOp",EDGE,"E7.sketch_text.stroke-97"),sQuery(id+"F6.wireOp",EDGE,"E7.sketch_text.stroke-98"),sQuery(id+"F6.wireOp",EDGE,"E7.sketch_text.stroke-99"),sQuery(id+"F6.wireOp",EDGE,"E7.sketch_text.stroke-100"),sQuery(id+"F6.wireOp",EDGE,"E7.sketch_text.stroke-101"),sQuery(id+"F6.wireOp",EDGE,"E7.sketch_text.stroke-102"),sQuery(id+"F6.wireOp",EDGE,"E7.sketch_text.stroke-103"),sQuery(id+"F6.wireOp",EDGE,"E7.sketch_text.stroke-104"),sQuery(id+"F6.wireOp",EDGE,"E7.sketch_text.stroke-105"),sQuery(id+"F6.wireOp",EDGE,"E7.sketch_text.stroke-106"),sQuery(id+"F6.wireOp",EDGE,"E7.sketch_text.stroke-107"),sQuery(id+"F6.wireOp",EDGE,"E7.sketch_text.stroke-108"),sQuery(id+"F6.wireOp",EDGE,"E7.sketch_text.stroke-109"),sQuery(id+"F6.wireOp",EDGE,"E7.sketch_text.stroke-110"),sQuery(id+"F6.wireOp",EDGE,"E7.sketch_text.stroke-111")])]});
            var Q5;
            Q5=makeQuery(id+"F9.opExtrude","SWEPT_BODY",BODY,{"disambiguationData":[OSD([sQuery(id+"F6.wireOp",EDGE,"E7.sketch_text.stroke-112"),sQuery(id+"F6.wireOp",EDGE,"E7.sketch_text.stroke-113"),sQuery(id+"F6.wireOp",EDGE,"E7.sketch_text.stroke-114"),sQuery(id+"F6.wireOp",EDGE,"E7.sketch_text.stroke-115"),sQuery(id+"F6.wireOp",EDGE,"E7.sketch_text.stroke-116"),sQuery(id+"F6.wireOp",EDGE,"E7.sketch_text.stroke-117"),sQuery(id+"F6.wireOp",EDGE,"E7.sketch_text.stroke-118"),sQuery(id+"F6.wireOp",EDGE,"E7.sketch_text.stroke-119"),sQuery(id+"F6.wireOp",EDGE,"E7.sketch_text.stroke-120"),sQuery(id+"F6.wireOp",EDGE,"E7.sketch_text.stroke-121"),sQuery(id+"F6.wireOp",EDGE,"E7.sketch_text.stroke-122"),sQuery(id+"F6.wireOp",EDGE,"E7.sketch_text.stroke-123"),sQuery(id+"F6.wireOp",EDGE,"E7.sketch_text.stroke-124"),sQuery(id+"F6.wireOp",EDGE,"E7.sketch_text.stroke-125"),sQuery(id+"F6.wireOp",EDGE,"E7.sketch_text.stroke-126"),sQuery(id+"F6.wireOp",EDGE,"E7.sketch_text.stroke-127"),sQuery(id+"F6.wireOp",EDGE,"E7.sketch_text.stroke-128"),sQuery(id+"F6.wireOp",EDGE,"E7.sketch_text.stroke-129"),sQuery(id+"F6.wireOp",EDGE,"E7.sketch_text.stroke-130"),sQuery(id+"F6.wireOp",EDGE,"E7.sketch_text.stroke-131"),sQuery(id+"F6.wireOp",EDGE,"E7.sketch_text.stroke-132"),sQuery(id+"F6.wireOp",EDGE,"E7.sketch_text.stroke-133"),sQuery(id+"F6.wireOp",EDGE,"E7.sketch_text.stroke-134"),sQuery(id+"F6.wireOp",EDGE,"E7.sketch_text.stroke-135"),sQuery(id+"F6.wireOp",EDGE,"E7.sketch_text.stroke-136"),sQuery(id+"F6.wireOp",EDGE,"E7.sketch_text.stroke-137")])]});
            var Q6;
            Q6=makeQuery(id+"F9.opExtrude","SWEPT_BODY",BODY,{"disambiguationData":[OSD([sQuery(id+"F6.wireOp",EDGE,"E7.sketch_text.stroke-138"),sQuery(id+"F6.wireOp",EDGE,"E7.sketch_text.stroke-139"),sQuery(id+"F6.wireOp",EDGE,"E7.sketch_text.stroke-140"),sQuery(id+"F6.wireOp",EDGE,"E7.sketch_text.stroke-141"),sQuery(id+"F6.wireOp",EDGE,"E7.sketch_text.stroke-142"),sQuery(id+"F6.wireOp",EDGE,"E7.sketch_text.stroke-143"),sQuery(id+"F6.wireOp",EDGE,"E7.sketch_text.stroke-144"),sQuery(id+"F6.wireOp",EDGE,"E7.sketch_text.stroke-145"),sQuery(id+"F6.wireOp",EDGE,"E7.sketch_text.stroke-146"),sQuery(id+"F6.wireOp",EDGE,"E7.sketch_text.stroke-147"),sQuery(id+"F6.wireOp",EDGE,"E7.sketch_text.stroke-148"),sQuery(id+"F6.wireOp",EDGE,"E7.sketch_text.stroke-149"),sQuery(id+"F6.wireOp",EDGE,"E7.sketch_text.stroke-150"),sQuery(id+"F6.wireOp",EDGE,"E7.sketch_text.stroke-151"),sQuery(id+"F6.wireOp",EDGE,"E7.sketch_text.stroke-152"),sQuery(id+"F6.wireOp",EDGE,"E7.sketch_text.stroke-153"),sQuery(id+"F6.wireOp",EDGE,"E7.sketch_text.stroke-154"),sQuery(id+"F6.wireOp",EDGE,"E7.sketch_text.stroke-155"),sQuery(id+"F6.wireOp",EDGE,"E7.sketch_text.stroke-156"),sQuery(id+"F6.wireOp",EDGE,"E7.sketch_text.stroke-157"),sQuery(id+"F6.wireOp",EDGE,"E7.sketch_text.stroke-158"),sQuery(id+"F6.wireOp",EDGE,"E7.sketch_text.stroke-159"),sQuery(id+"F6.wireOp",EDGE,"E7.sketch_text.stroke-160"),sQuery(id+"F6.wireOp",EDGE,"E7.sketch_text.stroke-161"),sQuery(id+"F6.wireOp",EDGE,"E7.sketch_text.stroke-162"),sQuery(id+"F6.wireOp",EDGE,"E7.sketch_text.stroke-163"),sQuery(id+"F6.wireOp",EDGE,"E7.sketch_text.stroke-164")])]});
            var Q7;
            Q7=makeQuery(id+"F9.opExtrude","SWEPT_BODY",BODY,{"disambiguationData":[OSD([sQuery(id+"F6.wireOp",EDGE,"E7.sketch_text.stroke-165"),sQuery(id+"F6.wireOp",EDGE,"E7.sketch_text.stroke-166"),sQuery(id+"F6.wireOp",EDGE,"E7.sketch_text.stroke-167"),sQuery(id+"F6.wireOp",EDGE,"E7.sketch_text.stroke-168"),sQuery(id+"F6.wireOp",EDGE,"E7.sketch_text.stroke-169"),sQuery(id+"F6.wireOp",EDGE,"E7.sketch_text.stroke-170"),sQuery(id+"F6.wireOp",EDGE,"E7.sketch_text.stroke-171"),sQuery(id+"F6.wireOp",EDGE,"E7.sketch_text.stroke-172"),sQuery(id+"F6.wireOp",EDGE,"E7.sketch_text.stroke-173"),sQuery(id+"F6.wireOp",EDGE,"E7.sketch_text.stroke-174"),sQuery(id+"F6.wireOp",EDGE,"E7.sketch_text.stroke-175"),sQuery(id+"F6.wireOp",EDGE,"E7.sketch_text.stroke-176"),sQuery(id+"F6.wireOp",EDGE,"E7.sketch_text.stroke-177"),sQuery(id+"F6.wireOp",EDGE,"E7.sketch_text.stroke-178"),sQuery(id+"F6.wireOp",EDGE,"E7.sketch_text.stroke-179"),sQuery(id+"F6.wireOp",EDGE,"E7.sketch_text.stroke-180"),sQuery(id+"F6.wireOp",EDGE,"E7.sketch_text.stroke-181"),sQuery(id+"F6.wireOp",EDGE,"E7.sketch_text.stroke-182"),sQuery(id+"F6.wireOp",EDGE,"E7.sketch_text.stroke-183"),sQuery(id+"F6.wireOp",EDGE,"E7.sketch_text.stroke-184")])]});
            var Q8;
            Q8=makeQuery(id+"F9.opExtrude","SWEPT_BODY",BODY,{"disambiguationData":[OSD([sQuery(id+"F7.wireOp",EDGE,"E9.sketch_text.stroke-0"),sQuery(id+"F7.wireOp",EDGE,"E9.sketch_text.stroke-1"),sQuery(id+"F7.wireOp",EDGE,"E9.sketch_text.stroke-2"),sQuery(id+"F7.wireOp",EDGE,"E9.sketch_text.stroke-3"),sQuery(id+"F7.wireOp",EDGE,"E9.sketch_text.stroke-4"),sQuery(id+"F7.wireOp",EDGE,"E9.sketch_text.stroke-5"),sQuery(id+"F7.wireOp",EDGE,"E9.sketch_text.stroke-6"),sQuery(id+"F7.wireOp",EDGE,"E9.sketch_text.stroke-7"),sQuery(id+"F7.wireOp",EDGE,"E9.sketch_text.stroke-8"),sQuery(id+"F7.wireOp",EDGE,"E9.sketch_text.stroke-9"),sQuery(id+"F7.wireOp",EDGE,"E9.sketch_text.stroke-10"),sQuery(id+"F7.wireOp",EDGE,"E9.sketch_text.stroke-11"),sQuery(id+"F7.wireOp",EDGE,"E9.sketch_text.stroke-12"),sQuery(id+"F7.wireOp",EDGE,"E9.sketch_text.stroke-13"),sQuery(id+"F7.wireOp",EDGE,"E9.sketch_text.stroke-14"),sQuery(id+"F7.wireOp",EDGE,"E9.sketch_text.stroke-15"),sQuery(id+"F7.wireOp",EDGE,"E9.sketch_text.stroke-16"),sQuery(id+"F7.wireOp",EDGE,"E9.sketch_text.stroke-17"),sQuery(id+"F7.wireOp",EDGE,"E9.sketch_text.stroke-18"),sQuery(id+"F7.wireOp",EDGE,"E9.sketch_text.stroke-19"),sQuery(id+"F7.wireOp",EDGE,"E9.sketch_text.stroke-20"),sQuery(id+"F7.wireOp",EDGE,"E9.sketch_text.stroke-21"),sQuery(id+"F7.wireOp",EDGE,"E9.sketch_text.stroke-22"),sQuery(id+"F7.wireOp",EDGE,"E9.sketch_text.stroke-23"),sQuery(id+"F7.wireOp",EDGE,"E9.sketch_text.stroke-24"),sQuery(id+"F7.wireOp",EDGE,"E9.sketch_text.stroke-25"),sQuery(id+"F7.wireOp",EDGE,"E9.sketch_text.stroke-26"),sQuery(id+"F7.wireOp",EDGE,"E9.sketch_text.stroke-27"),sQuery(id+"F7.wireOp",EDGE,"E9.sketch_text.stroke-28"),sQuery(id+"F7.wireOp",EDGE,"E9.sketch_text.stroke-29")])]});
            var Q9;
            Q9=makeQuery(id+"F9.opExtrude","SWEPT_BODY",BODY,{"disambiguationData":[OSD([sQuery(id+"F7.wireOp",EDGE,"E9.sketch_text.stroke-30"),sQuery(id+"F7.wireOp",EDGE,"E9.sketch_text.stroke-31"),sQuery(id+"F7.wireOp",EDGE,"E9.sketch_text.stroke-32"),sQuery(id+"F7.wireOp",EDGE,"E9.sketch_text.stroke-33"),sQuery(id+"F7.wireOp",EDGE,"E9.sketch_text.stroke-34"),sQuery(id+"F7.wireOp",EDGE,"E9.sketch_text.stroke-35"),sQuery(id+"F7.wireOp",EDGE,"E9.sketch_text.stroke-36"),sQuery(id+"F7.wireOp",EDGE,"E9.sketch_text.stroke-37"),sQuery(id+"F7.wireOp",EDGE,"E9.sketch_text.stroke-38"),sQuery(id+"F7.wireOp",EDGE,"E9.sketch_text.stroke-39"),sQuery(id+"F7.wireOp",EDGE,"E9.sketch_text.stroke-40"),sQuery(id+"F7.wireOp",EDGE,"E9.sketch_text.stroke-41"),sQuery(id+"F7.wireOp",EDGE,"E9.sketch_text.stroke-42"),sQuery(id+"F7.wireOp",EDGE,"E9.sketch_text.stroke-43"),sQuery(id+"F7.wireOp",EDGE,"E9.sketch_text.stroke-44"),sQuery(id+"F7.wireOp",EDGE,"E9.sketch_text.stroke-45"),sQuery(id+"F7.wireOp",EDGE,"E9.sketch_text.stroke-46"),sQuery(id+"F7.wireOp",EDGE,"E9.sketch_text.stroke-47"),sQuery(id+"F7.wireOp",EDGE,"E9.sketch_text.stroke-48"),sQuery(id+"F7.wireOp",EDGE,"E9.sketch_text.stroke-49")])]});
            var Q10;
            Q10=makeQuery(id+"F9.opExtrude","SWEPT_BODY",BODY,{"disambiguationData":[OSD([sQuery(id+"F7.wireOp",EDGE,"E9.sketch_text.stroke-50"),sQuery(id+"F7.wireOp",EDGE,"E9.sketch_text.stroke-51"),sQuery(id+"F7.wireOp",EDGE,"E9.sketch_text.stroke-52"),sQuery(id+"F7.wireOp",EDGE,"E9.sketch_text.stroke-53"),sQuery(id+"F7.wireOp",EDGE,"E9.sketch_text.stroke-54"),sQuery(id+"F7.wireOp",EDGE,"E9.sketch_text.stroke-55"),sQuery(id+"F7.wireOp",EDGE,"E9.sketch_text.stroke-56"),sQuery(id+"F7.wireOp",EDGE,"E9.sketch_text.stroke-57"),sQuery(id+"F7.wireOp",EDGE,"E9.sketch_text.stroke-58"),sQuery(id+"F7.wireOp",EDGE,"E9.sketch_text.stroke-59"),sQuery(id+"F7.wireOp",EDGE,"E9.sketch_text.stroke-60"),sQuery(id+"F7.wireOp",EDGE,"E9.sketch_text.stroke-61"),sQuery(id+"F7.wireOp",EDGE,"E9.sketch_text.stroke-62"),sQuery(id+"F7.wireOp",EDGE,"E9.sketch_text.stroke-63"),sQuery(id+"F7.wireOp",EDGE,"E9.sketch_text.stroke-64"),sQuery(id+"F7.wireOp",EDGE,"E9.sketch_text.stroke-65"),sQuery(id+"F7.wireOp",EDGE,"E9.sketch_text.stroke-66"),sQuery(id+"F7.wireOp",EDGE,"E9.sketch_text.stroke-67"),sQuery(id+"F7.wireOp",EDGE,"E9.sketch_text.stroke-68"),sQuery(id+"F7.wireOp",EDGE,"E9.sketch_text.stroke-69"),sQuery(id+"F7.wireOp",EDGE,"E9.sketch_text.stroke-70"),sQuery(id+"F7.wireOp",EDGE,"E9.sketch_text.stroke-71"),sQuery(id+"F7.wireOp",EDGE,"E9.sketch_text.stroke-72"),sQuery(id+"F7.wireOp",EDGE,"E9.sketch_text.stroke-73"),sQuery(id+"F7.wireOp",EDGE,"E9.sketch_text.stroke-74"),sQuery(id+"F7.wireOp",EDGE,"E9.sketch_text.stroke-75"),sQuery(id+"F7.wireOp",EDGE,"E9.sketch_text.stroke-76"),sQuery(id+"F7.wireOp",EDGE,"E9.sketch_text.stroke-77"),sQuery(id+"F7.wireOp",EDGE,"E9.sketch_text.stroke-78"),sQuery(id+"F7.wireOp",EDGE,"E9.sketch_text.stroke-79"),sQuery(id+"F7.wireOp",EDGE,"E9.sketch_text.stroke-80"),sQuery(id+"F7.wireOp",EDGE,"E9.sketch_text.stroke-81"),sQuery(id+"F7.wireOp",EDGE,"E9.sketch_text.stroke-82"),sQuery(id+"F7.wireOp",EDGE,"E9.sketch_text.stroke-83"),sQuery(id+"F7.wireOp",EDGE,"E9.sketch_text.stroke-84")])]});
            var Q11;
            Q11=makeQuery(id+"F9.opExtrude","SWEPT_BODY",BODY,{"disambiguationData":[OSD([sQuery(id+"F7.wireOp",EDGE,"E9.sketch_text.stroke-85"),sQuery(id+"F7.wireOp",EDGE,"E9.sketch_text.stroke-86"),sQuery(id+"F7.wireOp",EDGE,"E9.sketch_text.stroke-87"),sQuery(id+"F7.wireOp",EDGE,"E9.sketch_text.stroke-88"),sQuery(id+"F7.wireOp",EDGE,"E9.sketch_text.stroke-89"),sQuery(id+"F7.wireOp",EDGE,"E9.sketch_text.stroke-90"),sQuery(id+"F7.wireOp",EDGE,"E9.sketch_text.stroke-91"),sQuery(id+"F7.wireOp",EDGE,"E9.sketch_text.stroke-92"),sQuery(id+"F7.wireOp",EDGE,"E9.sketch_text.stroke-93"),sQuery(id+"F7.wireOp",EDGE,"E9.sketch_text.stroke-94"),sQuery(id+"F7.wireOp",EDGE,"E9.sketch_text.stroke-95"),sQuery(id+"F7.wireOp",EDGE,"E9.sketch_text.stroke-96"),sQuery(id+"F7.wireOp",EDGE,"E9.sketch_text.stroke-97"),sQuery(id+"F7.wireOp",EDGE,"E9.sketch_text.stroke-98"),sQuery(id+"F7.wireOp",EDGE,"E9.sketch_text.stroke-99"),sQuery(id+"F7.wireOp",EDGE,"E9.sketch_text.stroke-100"),sQuery(id+"F7.wireOp",EDGE,"E9.sketch_text.stroke-101"),sQuery(id+"F7.wireOp",EDGE,"E9.sketch_text.stroke-102"),sQuery(id+"F7.wireOp",EDGE,"E9.sketch_text.stroke-103")])]});
            var Q12;
            Q12=makeQuery(id+"F9.opExtrude","SWEPT_BODY",BODY,{"disambiguationData":[OSD([sQuery(id+"F7.wireOp",EDGE,"E9.sketch_text.stroke-104"),sQuery(id+"F7.wireOp",EDGE,"E9.sketch_text.stroke-105"),sQuery(id+"F7.wireOp",EDGE,"E9.sketch_text.stroke-106"),sQuery(id+"F7.wireOp",EDGE,"E9.sketch_text.stroke-107"),sQuery(id+"F7.wireOp",EDGE,"E9.sketch_text.stroke-108"),sQuery(id+"F7.wireOp",EDGE,"E9.sketch_text.stroke-109"),sQuery(id+"F7.wireOp",EDGE,"E9.sketch_text.stroke-110"),sQuery(id+"F7.wireOp",EDGE,"E9.sketch_text.stroke-111"),sQuery(id+"F7.wireOp",EDGE,"E9.sketch_text.stroke-112"),sQuery(id+"F7.wireOp",EDGE,"E9.sketch_text.stroke-113"),sQuery(id+"F7.wireOp",EDGE,"E9.sketch_text.stroke-114"),sQuery(id+"F7.wireOp",EDGE,"E9.sketch_text.stroke-115"),sQuery(id+"F7.wireOp",EDGE,"E9.sketch_text.stroke-116"),sQuery(id+"F7.wireOp",EDGE,"E9.sketch_text.stroke-117"),sQuery(id+"F7.wireOp",EDGE,"E9.sketch_text.stroke-118"),sQuery(id+"F7.wireOp",EDGE,"E9.sketch_text.stroke-119"),sQuery(id+"F7.wireOp",EDGE,"E9.sketch_text.stroke-120"),sQuery(id+"F7.wireOp",EDGE,"E9.sketch_text.stroke-121"),sQuery(id+"F7.wireOp",EDGE,"E9.sketch_text.stroke-122"),sQuery(id+"F7.wireOp",EDGE,"E9.sketch_text.stroke-123"),sQuery(id+"F7.wireOp",EDGE,"E9.sketch_text.stroke-124"),sQuery(id+"F7.wireOp",EDGE,"E9.sketch_text.stroke-125"),sQuery(id+"F7.wireOp",EDGE,"E9.sketch_text.stroke-126"),sQuery(id+"F7.wireOp",EDGE,"E9.sketch_text.stroke-127"),sQuery(id+"F7.wireOp",EDGE,"E9.sketch_text.stroke-128"),sQuery(id+"F7.wireOp",EDGE,"E9.sketch_text.stroke-129"),sQuery(id+"F7.wireOp",EDGE,"E9.sketch_text.stroke-130"),sQuery(id+"F7.wireOp",EDGE,"E9.sketch_text.stroke-131"),sQuery(id+"F7.wireOp",EDGE,"E9.sketch_text.stroke-132"),sQuery(id+"F7.wireOp",EDGE,"E9.sketch_text.stroke-133")])]});
            var Q13;
            Q13=makeQuery(id+"F9.opExtrude","SWEPT_BODY",BODY,{"disambiguationData":[OSD([sQuery(id+"FDBskpxBvZGabAj_3.wireOp",EDGE,"14cc8964-4ceb-4e8c-bfe6-0e7e09cf8f31.sketch_text.stroke-0"),sQuery(id+"FDBskpxBvZGabAj_3.wireOp",EDGE,"14cc8964-4ceb-4e8c-bfe6-0e7e09cf8f31.sketch_text.stroke-1"),sQuery(id+"FDBskpxBvZGabAj_3.wireOp",EDGE,"14cc8964-4ceb-4e8c-bfe6-0e7e09cf8f31.sketch_text.stroke-2"),sQuery(id+"FDBskpxBvZGabAj_3.wireOp",EDGE,"14cc8964-4ceb-4e8c-bfe6-0e7e09cf8f31.sketch_text.stroke-3"),sQuery(id+"FDBskpxBvZGabAj_3.wireOp",EDGE,"14cc8964-4ceb-4e8c-bfe6-0e7e09cf8f31.sketch_text.stroke-4"),sQuery(id+"FDBskpxBvZGabAj_3.wireOp",EDGE,"14cc8964-4ceb-4e8c-bfe6-0e7e09cf8f31.sketch_text.stroke-5"),sQuery(id+"FDBskpxBvZGabAj_3.wireOp",EDGE,"14cc8964-4ceb-4e8c-bfe6-0e7e09cf8f31.sketch_text.stroke-6"),sQuery(id+"FDBskpxBvZGabAj_3.wireOp",EDGE,"14cc8964-4ceb-4e8c-bfe6-0e7e09cf8f31.sketch_text.stroke-7"),sQuery(id+"FDBskpxBvZGabAj_3.wireOp",EDGE,"14cc8964-4ceb-4e8c-bfe6-0e7e09cf8f31.sketch_text.stroke-8"),sQuery(id+"FDBskpxBvZGabAj_3.wireOp",EDGE,"14cc8964-4ceb-4e8c-bfe6-0e7e09cf8f31.sketch_text.stroke-9"),sQuery(id+"FDBskpxBvZGabAj_3.wireOp",EDGE,"14cc8964-4ceb-4e8c-bfe6-0e7e09cf8f31.sketch_text.stroke-10"),sQuery(id+"FDBskpxBvZGabAj_3.wireOp",EDGE,"14cc8964-4ceb-4e8c-bfe6-0e7e09cf8f31.sketch_text.stroke-11"),sQuery(id+"FDBskpxBvZGabAj_3.wireOp",EDGE,"14cc8964-4ceb-4e8c-bfe6-0e7e09cf8f31.sketch_text.stroke-12"),sQuery(id+"FDBskpxBvZGabAj_3.wireOp",EDGE,"14cc8964-4ceb-4e8c-bfe6-0e7e09cf8f31.sketch_text.stroke-13"),sQuery(id+"FDBskpxBvZGabAj_3.wireOp",EDGE,"14cc8964-4ceb-4e8c-bfe6-0e7e09cf8f31.sketch_text.stroke-14"),sQuery(id+"FDBskpxBvZGabAj_3.wireOp",EDGE,"14cc8964-4ceb-4e8c-bfe6-0e7e09cf8f31.sketch_text.stroke-15"),sQuery(id+"FDBskpxBvZGabAj_3.wireOp",EDGE,"14cc8964-4ceb-4e8c-bfe6-0e7e09cf8f31.sketch_text.stroke-16"),sQuery(id+"FDBskpxBvZGabAj_3.wireOp",EDGE,"14cc8964-4ceb-4e8c-bfe6-0e7e09cf8f31.sketch_text.stroke-17"),sQuery(id+"FDBskpxBvZGabAj_3.wireOp",EDGE,"14cc8964-4ceb-4e8c-bfe6-0e7e09cf8f31.sketch_text.stroke-18"),sQuery(id+"FDBskpxBvZGabAj_3.wireOp",EDGE,"14cc8964-4ceb-4e8c-bfe6-0e7e09cf8f31.sketch_text.stroke-19"),sQuery(id+"FDBskpxBvZGabAj_3.wireOp",EDGE,"14cc8964-4ceb-4e8c-bfe6-0e7e09cf8f31.sketch_text.stroke-20"),sQuery(id+"FDBskpxBvZGabAj_3.wireOp",EDGE,"14cc8964-4ceb-4e8c-bfe6-0e7e09cf8f31.sketch_text.stroke-21"),sQuery(id+"FDBskpxBvZGabAj_3.wireOp",EDGE,"14cc8964-4ceb-4e8c-bfe6-0e7e09cf8f31.sketch_text.stroke-22")])]});
            var Q14;
            Q14=makeQuery(id+"F9.opExtrude","SWEPT_BODY",BODY,{"disambiguationData":[OSD([sQuery(id+"FDBskpxBvZGabAj_3.wireOp",EDGE,"14cc8964-4ceb-4e8c-bfe6-0e7e09cf8f31.sketch_text.stroke-23"),sQuery(id+"FDBskpxBvZGabAj_3.wireOp",EDGE,"14cc8964-4ceb-4e8c-bfe6-0e7e09cf8f31.sketch_text.stroke-24"),sQuery(id+"FDBskpxBvZGabAj_3.wireOp",EDGE,"14cc8964-4ceb-4e8c-bfe6-0e7e09cf8f31.sketch_text.stroke-25"),sQuery(id+"FDBskpxBvZGabAj_3.wireOp",EDGE,"14cc8964-4ceb-4e8c-bfe6-0e7e09cf8f31.sketch_text.stroke-26"),sQuery(id+"FDBskpxBvZGabAj_3.wireOp",EDGE,"14cc8964-4ceb-4e8c-bfe6-0e7e09cf8f31.sketch_text.stroke-27"),sQuery(id+"FDBskpxBvZGabAj_3.wireOp",EDGE,"14cc8964-4ceb-4e8c-bfe6-0e7e09cf8f31.sketch_text.stroke-28"),sQuery(id+"FDBskpxBvZGabAj_3.wireOp",EDGE,"14cc8964-4ceb-4e8c-bfe6-0e7e09cf8f31.sketch_text.stroke-29"),sQuery(id+"FDBskpxBvZGabAj_3.wireOp",EDGE,"14cc8964-4ceb-4e8c-bfe6-0e7e09cf8f31.sketch_text.stroke-30"),sQuery(id+"FDBskpxBvZGabAj_3.wireOp",EDGE,"14cc8964-4ceb-4e8c-bfe6-0e7e09cf8f31.sketch_text.stroke-31"),sQuery(id+"FDBskpxBvZGabAj_3.wireOp",EDGE,"14cc8964-4ceb-4e8c-bfe6-0e7e09cf8f31.sketch_text.stroke-32"),sQuery(id+"FDBskpxBvZGabAj_3.wireOp",EDGE,"14cc8964-4ceb-4e8c-bfe6-0e7e09cf8f31.sketch_text.stroke-33"),sQuery(id+"FDBskpxBvZGabAj_3.wireOp",EDGE,"14cc8964-4ceb-4e8c-bfe6-0e7e09cf8f31.sketch_text.stroke-34"),sQuery(id+"FDBskpxBvZGabAj_3.wireOp",EDGE,"14cc8964-4ceb-4e8c-bfe6-0e7e09cf8f31.sketch_text.stroke-35"),sQuery(id+"FDBskpxBvZGabAj_3.wireOp",EDGE,"14cc8964-4ceb-4e8c-bfe6-0e7e09cf8f31.sketch_text.stroke-36"),sQuery(id+"FDBskpxBvZGabAj_3.wireOp",EDGE,"14cc8964-4ceb-4e8c-bfe6-0e7e09cf8f31.sketch_text.stroke-37"),sQuery(id+"FDBskpxBvZGabAj_3.wireOp",EDGE,"14cc8964-4ceb-4e8c-bfe6-0e7e09cf8f31.sketch_text.stroke-38"),sQuery(id+"FDBskpxBvZGabAj_3.wireOp",EDGE,"14cc8964-4ceb-4e8c-bfe6-0e7e09cf8f31.sketch_text.stroke-39"),sQuery(id+"FDBskpxBvZGabAj_3.wireOp",EDGE,"14cc8964-4ceb-4e8c-bfe6-0e7e09cf8f31.sketch_text.stroke-40"),sQuery(id+"FDBskpxBvZGabAj_3.wireOp",EDGE,"14cc8964-4ceb-4e8c-bfe6-0e7e09cf8f31.sketch_text.stroke-41"),sQuery(id+"FDBskpxBvZGabAj_3.wireOp",EDGE,"14cc8964-4ceb-4e8c-bfe6-0e7e09cf8f31.sketch_text.stroke-42")])]});
            var Q15;
            Q15=makeQuery(id+"F9.opExtrude","SWEPT_BODY",BODY,{"disambiguationData":[OSD([sQuery(id+"FDBskpxBvZGabAj_3.wireOp",EDGE,"14cc8964-4ceb-4e8c-bfe6-0e7e09cf8f31.sketch_text.stroke-43"),sQuery(id+"FDBskpxBvZGabAj_3.wireOp",EDGE,"14cc8964-4ceb-4e8c-bfe6-0e7e09cf8f31.sketch_text.stroke-44"),sQuery(id+"FDBskpxBvZGabAj_3.wireOp",EDGE,"14cc8964-4ceb-4e8c-bfe6-0e7e09cf8f31.sketch_text.stroke-45"),sQuery(id+"FDBskpxBvZGabAj_3.wireOp",EDGE,"14cc8964-4ceb-4e8c-bfe6-0e7e09cf8f31.sketch_text.stroke-46"),sQuery(id+"FDBskpxBvZGabAj_3.wireOp",EDGE,"14cc8964-4ceb-4e8c-bfe6-0e7e09cf8f31.sketch_text.stroke-47"),sQuery(id+"FDBskpxBvZGabAj_3.wireOp",EDGE,"14cc8964-4ceb-4e8c-bfe6-0e7e09cf8f31.sketch_text.stroke-48"),sQuery(id+"FDBskpxBvZGabAj_3.wireOp",EDGE,"14cc8964-4ceb-4e8c-bfe6-0e7e09cf8f31.sketch_text.stroke-49"),sQuery(id+"FDBskpxBvZGabAj_3.wireOp",EDGE,"14cc8964-4ceb-4e8c-bfe6-0e7e09cf8f31.sketch_text.stroke-50"),sQuery(id+"FDBskpxBvZGabAj_3.wireOp",EDGE,"14cc8964-4ceb-4e8c-bfe6-0e7e09cf8f31.sketch_text.stroke-51"),sQuery(id+"FDBskpxBvZGabAj_3.wireOp",EDGE,"14cc8964-4ceb-4e8c-bfe6-0e7e09cf8f31.sketch_text.stroke-52")])]});
            var Q16;
            Q16=makeQuery(id+"F9.opExtrude","SWEPT_BODY",BODY,{"disambiguationData":[OSD([sQuery(id+"FDBskpxBvZGabAj_3.wireOp",EDGE,"14cc8964-4ceb-4e8c-bfe6-0e7e09cf8f31.sketch_text.stroke-53"),sQuery(id+"FDBskpxBvZGabAj_3.wireOp",EDGE,"14cc8964-4ceb-4e8c-bfe6-0e7e09cf8f31.sketch_text.stroke-54"),sQuery(id+"FDBskpxBvZGabAj_3.wireOp",EDGE,"14cc8964-4ceb-4e8c-bfe6-0e7e09cf8f31.sketch_text.stroke-55"),sQuery(id+"FDBskpxBvZGabAj_3.wireOp",EDGE,"14cc8964-4ceb-4e8c-bfe6-0e7e09cf8f31.sketch_text.stroke-56"),sQuery(id+"FDBskpxBvZGabAj_3.wireOp",EDGE,"14cc8964-4ceb-4e8c-bfe6-0e7e09cf8f31.sketch_text.stroke-57"),sQuery(id+"FDBskpxBvZGabAj_3.wireOp",EDGE,"14cc8964-4ceb-4e8c-bfe6-0e7e09cf8f31.sketch_text.stroke-58"),sQuery(id+"FDBskpxBvZGabAj_3.wireOp",EDGE,"14cc8964-4ceb-4e8c-bfe6-0e7e09cf8f31.sketch_text.stroke-59"),sQuery(id+"FDBskpxBvZGabAj_3.wireOp",EDGE,"14cc8964-4ceb-4e8c-bfe6-0e7e09cf8f31.sketch_text.stroke-60"),sQuery(id+"FDBskpxBvZGabAj_3.wireOp",EDGE,"14cc8964-4ceb-4e8c-bfe6-0e7e09cf8f31.sketch_text.stroke-61"),sQuery(id+"FDBskpxBvZGabAj_3.wireOp",EDGE,"14cc8964-4ceb-4e8c-bfe6-0e7e09cf8f31.sketch_text.stroke-62"),sQuery(id+"FDBskpxBvZGabAj_3.wireOp",EDGE,"14cc8964-4ceb-4e8c-bfe6-0e7e09cf8f31.sketch_text.stroke-63"),sQuery(id+"FDBskpxBvZGabAj_3.wireOp",EDGE,"14cc8964-4ceb-4e8c-bfe6-0e7e09cf8f31.sketch_text.stroke-64"),sQuery(id+"FDBskpxBvZGabAj_3.wireOp",EDGE,"14cc8964-4ceb-4e8c-bfe6-0e7e09cf8f31.sketch_text.stroke-65"),sQuery(id+"FDBskpxBvZGabAj_3.wireOp",EDGE,"14cc8964-4ceb-4e8c-bfe6-0e7e09cf8f31.sketch_text.stroke-66"),sQuery(id+"FDBskpxBvZGabAj_3.wireOp",EDGE,"14cc8964-4ceb-4e8c-bfe6-0e7e09cf8f31.sketch_text.stroke-67"),sQuery(id+"FDBskpxBvZGabAj_3.wireOp",EDGE,"14cc8964-4ceb-4e8c-bfe6-0e7e09cf8f31.sketch_text.stroke-68"),sQuery(id+"FDBskpxBvZGabAj_3.wireOp",EDGE,"14cc8964-4ceb-4e8c-bfe6-0e7e09cf8f31.sketch_text.stroke-69"),sQuery(id+"FDBskpxBvZGabAj_3.wireOp",EDGE,"14cc8964-4ceb-4e8c-bfe6-0e7e09cf8f31.sketch_text.stroke-70"),sQuery(id+"FDBskpxBvZGabAj_3.wireOp",EDGE,"14cc8964-4ceb-4e8c-bfe6-0e7e09cf8f31.sketch_text.stroke-71"),sQuery(id+"FDBskpxBvZGabAj_3.wireOp",EDGE,"14cc8964-4ceb-4e8c-bfe6-0e7e09cf8f31.sketch_text.stroke-72"),sQuery(id+"FDBskpxBvZGabAj_3.wireOp",EDGE,"14cc8964-4ceb-4e8c-bfe6-0e7e09cf8f31.sketch_text.stroke-73"),sQuery(id+"FDBskpxBvZGabAj_3.wireOp",EDGE,"14cc8964-4ceb-4e8c-bfe6-0e7e09cf8f31.sketch_text.stroke-74"),sQuery(id+"FDBskpxBvZGabAj_3.wireOp",EDGE,"14cc8964-4ceb-4e8c-bfe6-0e7e09cf8f31.sketch_text.stroke-75"),sQuery(id+"FDBskpxBvZGabAj_3.wireOp",EDGE,"14cc8964-4ceb-4e8c-bfe6-0e7e09cf8f31.sketch_text.stroke-76"),sQuery(id+"FDBskpxBvZGabAj_3.wireOp",EDGE,"14cc8964-4ceb-4e8c-bfe6-0e7e09cf8f31.sketch_text.stroke-77"),sQuery(id+"FDBskpxBvZGabAj_3.wireOp",EDGE,"14cc8964-4ceb-4e8c-bfe6-0e7e09cf8f31.sketch_text.stroke-78")])]});
            var Q17;
            Q17=makeQuery(id+"F9.opExtrude","SWEPT_BODY",BODY,{"disambiguationData":[OSD([sQuery(id+"FDBskpxBvZGabAj_3.wireOp",EDGE,"14cc8964-4ceb-4e8c-bfe6-0e7e09cf8f31.sketch_text.stroke-79"),sQuery(id+"FDBskpxBvZGabAj_3.wireOp",EDGE,"14cc8964-4ceb-4e8c-bfe6-0e7e09cf8f31.sketch_text.stroke-80"),sQuery(id+"FDBskpxBvZGabAj_3.wireOp",EDGE,"14cc8964-4ceb-4e8c-bfe6-0e7e09cf8f31.sketch_text.stroke-81"),sQuery(id+"FDBskpxBvZGabAj_3.wireOp",EDGE,"14cc8964-4ceb-4e8c-bfe6-0e7e09cf8f31.sketch_text.stroke-82")])]});
            var Q18;
            Q18=makeQuery(id+"F9.opExtrude","SWEPT_BODY",BODY,{"disambiguationData":[OSD([sQuery(id+"FDBskpxBvZGabAj_3.wireOp",EDGE,"14cc8964-4ceb-4e8c-bfe6-0e7e09cf8f31.sketch_text.stroke-83"),sQuery(id+"FDBskpxBvZGabAj_3.wireOp",EDGE,"14cc8964-4ceb-4e8c-bfe6-0e7e09cf8f31.sketch_text.stroke-84"),sQuery(id+"FDBskpxBvZGabAj_3.wireOp",EDGE,"14cc8964-4ceb-4e8c-bfe6-0e7e09cf8f31.sketch_text.stroke-85"),sQuery(id+"FDBskpxBvZGabAj_3.wireOp",EDGE,"14cc8964-4ceb-4e8c-bfe6-0e7e09cf8f31.sketch_text.stroke-86"),sQuery(id+"FDBskpxBvZGabAj_3.wireOp",EDGE,"14cc8964-4ceb-4e8c-bfe6-0e7e09cf8f31.sketch_text.stroke-87"),sQuery(id+"FDBskpxBvZGabAj_3.wireOp",EDGE,"14cc8964-4ceb-4e8c-bfe6-0e7e09cf8f31.sketch_text.stroke-88"),sQuery(id+"FDBskpxBvZGabAj_3.wireOp",EDGE,"14cc8964-4ceb-4e8c-bfe6-0e7e09cf8f31.sketch_text.stroke-89"),sQuery(id+"FDBskpxBvZGabAj_3.wireOp",EDGE,"14cc8964-4ceb-4e8c-bfe6-0e7e09cf8f31.sketch_text.stroke-90"),sQuery(id+"FDBskpxBvZGabAj_3.wireOp",EDGE,"14cc8964-4ceb-4e8c-bfe6-0e7e09cf8f31.sketch_text.stroke-91"),sQuery(id+"FDBskpxBvZGabAj_3.wireOp",EDGE,"14cc8964-4ceb-4e8c-bfe6-0e7e09cf8f31.sketch_text.stroke-92"),sQuery(id+"FDBskpxBvZGabAj_3.wireOp",EDGE,"14cc8964-4ceb-4e8c-bfe6-0e7e09cf8f31.sketch_text.stroke-93"),sQuery(id+"FDBskpxBvZGabAj_3.wireOp",EDGE,"14cc8964-4ceb-4e8c-bfe6-0e7e09cf8f31.sketch_text.stroke-94"),sQuery(id+"FDBskpxBvZGabAj_3.wireOp",EDGE,"14cc8964-4ceb-4e8c-bfe6-0e7e09cf8f31.sketch_text.stroke-95"),sQuery(id+"FDBskpxBvZGabAj_3.wireOp",EDGE,"14cc8964-4ceb-4e8c-bfe6-0e7e09cf8f31.sketch_text.stroke-96"),sQuery(id+"FDBskpxBvZGabAj_3.wireOp",EDGE,"14cc8964-4ceb-4e8c-bfe6-0e7e09cf8f31.sketch_text.stroke-97"),sQuery(id+"FDBskpxBvZGabAj_3.wireOp",EDGE,"14cc8964-4ceb-4e8c-bfe6-0e7e09cf8f31.sketch_text.stroke-98"),sQuery(id+"FDBskpxBvZGabAj_3.wireOp",EDGE,"14cc8964-4ceb-4e8c-bfe6-0e7e09cf8f31.sketch_text.stroke-99"),sQuery(id+"FDBskpxBvZGabAj_3.wireOp",EDGE,"14cc8964-4ceb-4e8c-bfe6-0e7e09cf8f31.sketch_text.stroke-100"),sQuery(id+"FDBskpxBvZGabAj_3.wireOp",EDGE,"14cc8964-4ceb-4e8c-bfe6-0e7e09cf8f31.sketch_text.stroke-101"),sQuery(id+"FDBskpxBvZGabAj_3.wireOp",EDGE,"14cc8964-4ceb-4e8c-bfe6-0e7e09cf8f31.sketch_text.stroke-102"),sQuery(id+"FDBskpxBvZGabAj_3.wireOp",EDGE,"14cc8964-4ceb-4e8c-bfe6-0e7e09cf8f31.sketch_text.stroke-103"),sQuery(id+"FDBskpxBvZGabAj_3.wireOp",EDGE,"14cc8964-4ceb-4e8c-bfe6-0e7e09cf8f31.sketch_text.stroke-104"),sQuery(id+"FDBskpxBvZGabAj_3.wireOp",EDGE,"14cc8964-4ceb-4e8c-bfe6-0e7e09cf8f31.sketch_text.stroke-105")])]});
            var Q19;
            Q19=makeQuery(id+"F9.opExtrude","SWEPT_BODY",BODY,{"disambiguationData":[OSD([sQuery(id+"FDBskpxBvZGabAj_3.wireOp",EDGE,"14cc8964-4ceb-4e8c-bfe6-0e7e09cf8f31.sketch_text.stroke-106"),sQuery(id+"FDBskpxBvZGabAj_3.wireOp",EDGE,"14cc8964-4ceb-4e8c-bfe6-0e7e09cf8f31.sketch_text.stroke-107"),sQuery(id+"FDBskpxBvZGabAj_3.wireOp",EDGE,"14cc8964-4ceb-4e8c-bfe6-0e7e09cf8f31.sketch_text.stroke-108"),sQuery(id+"FDBskpxBvZGabAj_3.wireOp",EDGE,"14cc8964-4ceb-4e8c-bfe6-0e7e09cf8f31.sketch_text.stroke-109"),sQuery(id+"FDBskpxBvZGabAj_3.wireOp",EDGE,"14cc8964-4ceb-4e8c-bfe6-0e7e09cf8f31.sketch_text.stroke-110"),sQuery(id+"FDBskpxBvZGabAj_3.wireOp",EDGE,"14cc8964-4ceb-4e8c-bfe6-0e7e09cf8f31.sketch_text.stroke-111"),sQuery(id+"FDBskpxBvZGabAj_3.wireOp",EDGE,"14cc8964-4ceb-4e8c-bfe6-0e7e09cf8f31.sketch_text.stroke-112"),sQuery(id+"FDBskpxBvZGabAj_3.wireOp",EDGE,"14cc8964-4ceb-4e8c-bfe6-0e7e09cf8f31.sketch_text.stroke-113"),sQuery(id+"FDBskpxBvZGabAj_3.wireOp",EDGE,"14cc8964-4ceb-4e8c-bfe6-0e7e09cf8f31.sketch_text.stroke-114"),sQuery(id+"FDBskpxBvZGabAj_3.wireOp",EDGE,"14cc8964-4ceb-4e8c-bfe6-0e7e09cf8f31.sketch_text.stroke-115"),sQuery(id+"FDBskpxBvZGabAj_3.wireOp",EDGE,"14cc8964-4ceb-4e8c-bfe6-0e7e09cf8f31.sketch_text.stroke-116"),sQuery(id+"FDBskpxBvZGabAj_3.wireOp",EDGE,"14cc8964-4ceb-4e8c-bfe6-0e7e09cf8f31.sketch_text.stroke-117"),sQuery(id+"FDBskpxBvZGabAj_3.wireOp",EDGE,"14cc8964-4ceb-4e8c-bfe6-0e7e09cf8f31.sketch_text.stroke-118"),sQuery(id+"FDBskpxBvZGabAj_3.wireOp",EDGE,"14cc8964-4ceb-4e8c-bfe6-0e7e09cf8f31.sketch_text.stroke-119"),sQuery(id+"FDBskpxBvZGabAj_3.wireOp",EDGE,"14cc8964-4ceb-4e8c-bfe6-0e7e09cf8f31.sketch_text.stroke-120"),sQuery(id+"FDBskpxBvZGabAj_3.wireOp",EDGE,"14cc8964-4ceb-4e8c-bfe6-0e7e09cf8f31.sketch_text.stroke-121"),sQuery(id+"FDBskpxBvZGabAj_3.wireOp",EDGE,"14cc8964-4ceb-4e8c-bfe6-0e7e09cf8f31.sketch_text.stroke-122"),sQuery(id+"FDBskpxBvZGabAj_3.wireOp",EDGE,"14cc8964-4ceb-4e8c-bfe6-0e7e09cf8f31.sketch_text.stroke-123"),sQuery(id+"FDBskpxBvZGabAj_3.wireOp",EDGE,"14cc8964-4ceb-4e8c-bfe6-0e7e09cf8f31.sketch_text.stroke-124"),sQuery(id+"FDBskpxBvZGabAj_3.wireOp",EDGE,"14cc8964-4ceb-4e8c-bfe6-0e7e09cf8f31.sketch_text.stroke-125")])]});
            var Q20;
            Q20=makeQuery(id+"F9.opExtrude","SWEPT_BODY",BODY,{"disambiguationData":[OSD([sQuery(id+"FDBskpxBvZGabAj_3.wireOp",EDGE,"14cc8964-4ceb-4e8c-bfe6-0e7e09cf8f31.sketch_text.stroke-126"),sQuery(id+"FDBskpxBvZGabAj_3.wireOp",EDGE,"14cc8964-4ceb-4e8c-bfe6-0e7e09cf8f31.sketch_text.stroke-127"),sQuery(id+"FDBskpxBvZGabAj_3.wireOp",EDGE,"14cc8964-4ceb-4e8c-bfe6-0e7e09cf8f31.sketch_text.stroke-128"),sQuery(id+"FDBskpxBvZGabAj_3.wireOp",EDGE,"14cc8964-4ceb-4e8c-bfe6-0e7e09cf8f31.sketch_text.stroke-129"),sQuery(id+"FDBskpxBvZGabAj_3.wireOp",EDGE,"14cc8964-4ceb-4e8c-bfe6-0e7e09cf8f31.sketch_text.stroke-130"),sQuery(id+"FDBskpxBvZGabAj_3.wireOp",EDGE,"14cc8964-4ceb-4e8c-bfe6-0e7e09cf8f31.sketch_text.stroke-131"),sQuery(id+"FDBskpxBvZGabAj_3.wireOp",EDGE,"14cc8964-4ceb-4e8c-bfe6-0e7e09cf8f31.sketch_text.stroke-132"),sQuery(id+"FDBskpxBvZGabAj_3.wireOp",EDGE,"14cc8964-4ceb-4e8c-bfe6-0e7e09cf8f31.sketch_text.stroke-133"),sQuery(id+"FDBskpxBvZGabAj_3.wireOp",EDGE,"14cc8964-4ceb-4e8c-bfe6-0e7e09cf8f31.sketch_text.stroke-134"),sQuery(id+"FDBskpxBvZGabAj_3.wireOp",EDGE,"14cc8964-4ceb-4e8c-bfe6-0e7e09cf8f31.sketch_text.stroke-135")])]});
            var Q21;
            Q21=makeQuery(id+"F9.opExtrude","SWEPT_BODY",BODY,{"disambiguationData":[OSD([sQuery(id+"FDBskpxBvZGabAj_3.wireOp",EDGE,"14cc8964-4ceb-4e8c-bfe6-0e7e09cf8f31.sketch_text.stroke-136"),sQuery(id+"FDBskpxBvZGabAj_3.wireOp",EDGE,"14cc8964-4ceb-4e8c-bfe6-0e7e09cf8f31.sketch_text.stroke-137"),sQuery(id+"FDBskpxBvZGabAj_3.wireOp",EDGE,"14cc8964-4ceb-4e8c-bfe6-0e7e09cf8f31.sketch_text.stroke-138"),sQuery(id+"FDBskpxBvZGabAj_3.wireOp",EDGE,"14cc8964-4ceb-4e8c-bfe6-0e7e09cf8f31.sketch_text.stroke-139"),sQuery(id+"FDBskpxBvZGabAj_3.wireOp",EDGE,"14cc8964-4ceb-4e8c-bfe6-0e7e09cf8f31.sketch_text.stroke-140"),sQuery(id+"FDBskpxBvZGabAj_3.wireOp",EDGE,"14cc8964-4ceb-4e8c-bfe6-0e7e09cf8f31.sketch_text.stroke-141"),sQuery(id+"FDBskpxBvZGabAj_3.wireOp",EDGE,"14cc8964-4ceb-4e8c-bfe6-0e7e09cf8f31.sketch_text.stroke-142"),sQuery(id+"FDBskpxBvZGabAj_3.wireOp",EDGE,"14cc8964-4ceb-4e8c-bfe6-0e7e09cf8f31.sketch_text.stroke-143"),sQuery(id+"FDBskpxBvZGabAj_3.wireOp",EDGE,"14cc8964-4ceb-4e8c-bfe6-0e7e09cf8f31.sketch_text.stroke-144"),sQuery(id+"FDBskpxBvZGabAj_3.wireOp",EDGE,"14cc8964-4ceb-4e8c-bfe6-0e7e09cf8f31.sketch_text.stroke-145"),sQuery(id+"FDBskpxBvZGabAj_3.wireOp",EDGE,"14cc8964-4ceb-4e8c-bfe6-0e7e09cf8f31.sketch_text.stroke-146"),sQuery(id+"FDBskpxBvZGabAj_3.wireOp",EDGE,"14cc8964-4ceb-4e8c-bfe6-0e7e09cf8f31.sketch_text.stroke-147"),sQuery(id+"FDBskpxBvZGabAj_3.wireOp",EDGE,"14cc8964-4ceb-4e8c-bfe6-0e7e09cf8f31.sketch_text.stroke-148"),sQuery(id+"FDBskpxBvZGabAj_3.wireOp",EDGE,"14cc8964-4ceb-4e8c-bfe6-0e7e09cf8f31.sketch_text.stroke-149"),sQuery(id+"FDBskpxBvZGabAj_3.wireOp",EDGE,"14cc8964-4ceb-4e8c-bfe6-0e7e09cf8f31.sketch_text.stroke-150"),sQuery(id+"FDBskpxBvZGabAj_3.wireOp",EDGE,"14cc8964-4ceb-4e8c-bfe6-0e7e09cf8f31.sketch_text.stroke-151"),sQuery(id+"FDBskpxBvZGabAj_3.wireOp",EDGE,"14cc8964-4ceb-4e8c-bfe6-0e7e09cf8f31.sketch_text.stroke-152"),sQuery(id+"FDBskpxBvZGabAj_3.wireOp",EDGE,"14cc8964-4ceb-4e8c-bfe6-0e7e09cf8f31.sketch_text.stroke-153"),sQuery(id+"FDBskpxBvZGabAj_3.wireOp",EDGE,"14cc8964-4ceb-4e8c-bfe6-0e7e09cf8f31.sketch_text.stroke-154"),sQuery(id+"FDBskpxBvZGabAj_3.wireOp",EDGE,"14cc8964-4ceb-4e8c-bfe6-0e7e09cf8f31.sketch_text.stroke-155"),sQuery(id+"FDBskpxBvZGabAj_3.wireOp",EDGE,"14cc8964-4ceb-4e8c-bfe6-0e7e09cf8f31.sketch_text.stroke-156"),sQuery(id+"FDBskpxBvZGabAj_3.wireOp",EDGE,"14cc8964-4ceb-4e8c-bfe6-0e7e09cf8f31.sketch_text.stroke-157"),sQuery(id+"FDBskpxBvZGabAj_3.wireOp",EDGE,"14cc8964-4ceb-4e8c-bfe6-0e7e09cf8f31.sketch_text.stroke-158"),sQuery(id+"FDBskpxBvZGabAj_3.wireOp",EDGE,"14cc8964-4ceb-4e8c-bfe6-0e7e09cf8f31.sketch_text.stroke-159"),sQuery(id+"FDBskpxBvZGabAj_3.wireOp",EDGE,"14cc8964-4ceb-4e8c-bfe6-0e7e09cf8f31.sketch_text.stroke-160"),sQuery(id+"FDBskpxBvZGabAj_3.wireOp",EDGE,"14cc8964-4ceb-4e8c-bfe6-0e7e09cf8f31.sketch_text.stroke-161"),sQuery(id+"FDBskpxBvZGabAj_3.wireOp",EDGE,"14cc8964-4ceb-4e8c-bfe6-0e7e09cf8f31.sketch_text.stroke-162"),sQuery(id+"FDBskpxBvZGabAj_3.wireOp",EDGE,"14cc8964-4ceb-4e8c-bfe6-0e7e09cf8f31.sketch_text.stroke-163")])]});
            var Q22;
            Q22=makeQuery(id+"F5.opBoolean","INTERSECT",BODY,{"derivedFrom":[makeQuery(id+"F1.opExtrude","SWEPT_BODY",BODY,{"disambiguationData":[OSD([sQuery(id+"F0.wireOp",EDGE,"E0"),sQuery(id+"F0.wireOp",EDGE,"E1"),sQuery(id+"F0.wireOp",EDGE,"E2"),sQuery(id+"F0.wireOp",EDGE,"E3"),sQuery(id+"F0.wireOp",EDGE,"E4")])]}),makeQuery(id+"F4.opRevolve","SWEPT_BODY",BODY,{"disambiguationData":[OSD([sQuery(id+"F2.wireOp",EDGE,"E5"),sQuery(id+"F2.wireOp",EDGE,"E6")])]})]});
            booleanBodies(context, id + "F11", {"operationType" : BooleanOperationType.SUBTRACTION, "tools" : qUnion([Q0, Q1, Q2, Q3, Q4, Q5, Q6, Q7, Q8, Q9, Q10, Q11, Q12, Q13, Q14, Q15, Q16, Q17, Q18, Q19, Q20, Q21]), "targets" : qUnion([Q22])});
        }
        {
            var Q0;
            Q0=qCreatedBy(makeId("Top.planeOp"),FACE);
            var sketch = newSketch(context, id + "F12", { "sketchPlane" : qUnion([Q0])});
            skCircle(sketch, "E10", {"center": v(0, 0) * mm, "radius": 19.69 * mm});
            skSolve(sketch);
        }
        {
            var Q0;
            Q0=makeQuery(id+"F12.imprint","IMPRINT",FACE,{"disambiguationData":[TD([[makeQuery(id+"F12.imprint","IMPRINT",EDGE,{"derivedFrom":sQuery(id+"F12.wireOp",EDGE,"E10")}),1.0]])]});
            var Q1;
            Q1=sQuery(id+"F12.wireOp",EDGE,"E10");
            extrude(context, id + "F13", {"entities" : qUnion([Q0]), "surfaceEntities" : qUnion([Q1]), "depth" : 6.35 * mm});
        }
        {
            var Q0;
            Q0=makeQuery(id+"F13.opExtrude","SWEPT_BODY",BODY,{"disambiguationData":[OSD([sQuery(id+"F12.wireOp",EDGE,"E10")])]});
            var Q1;
            Q1=makeQuery(id+"F1.opExtrude","CAP_FACE",FACE,{"disambiguationData":[OSD([sQuery(id+"F0.wireOp",EDGE,"E0"),sQuery(id+"F0.wireOp",EDGE,"E1"),sQuery(id+"F0.wireOp",EDGE,"E2"),sQuery(id+"F0.wireOp",EDGE,"E3"),sQuery(id+"F0.wireOp",EDGE,"E4")])],"isStart":true});
            transform(context, id + "F14", {"entities" : qUnion([Q0]), "transformType" : TransformType.TRANSLATION_DISTANCE, "transformDirection" : qUnion([Q1]), "distance" : 52.24 * mm, "makeCopy" : false});
        }
        {
            var Q0;
            Q0=makeQuery(id+"F13.opExtrude","SWEPT_BODY",BODY,{"disambiguationData":[OSD([sQuery(id+"F12.wireOp",EDGE,"E10")])]});
            var Q1;
            Q1=makeQuery(id+"F5.opBoolean","INTERSECT",BODY,{"derivedFrom":[makeQuery(id+"F1.opExtrude","SWEPT_BODY",BODY,{"disambiguationData":[OSD([sQuery(id+"F0.wireOp",EDGE,"E0"),sQuery(id+"F0.wireOp",EDGE,"E1"),sQuery(id+"F0.wireOp",EDGE,"E2"),sQuery(id+"F0.wireOp",EDGE,"E3"),sQuery(id+"F0.wireOp",EDGE,"E4")])]}),makeQuery(id+"F4.opRevolve","SWEPT_BODY",BODY,{"disambiguationData":[OSD([sQuery(id+"F2.wireOp",EDGE,"E5"),sQuery(id+"F2.wireOp",EDGE,"E6")])]})]});
            booleanBodies(context, id + "F15", {"operationType" : BooleanOperationType.SUBTRACTION, "tools" : qUnion([Q0]), "targets" : qUnion([Q1])});
        }
    });
